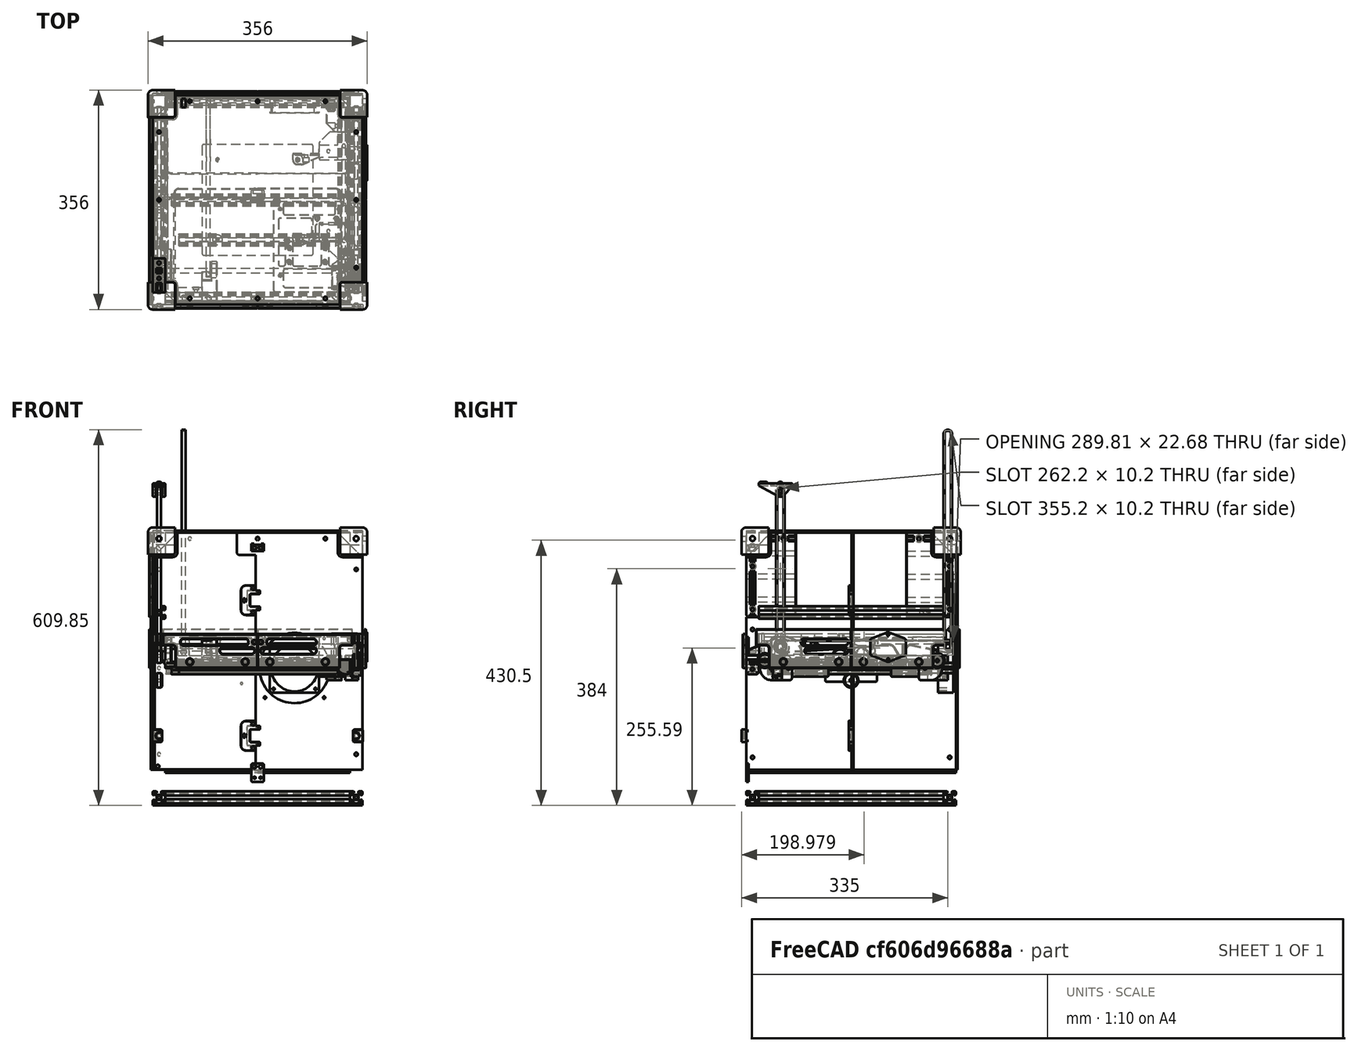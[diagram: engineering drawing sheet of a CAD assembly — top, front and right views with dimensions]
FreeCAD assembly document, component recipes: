
FREECAD ASSEMBLY — COMPONENT RECIPES ("assembly")

This assembly document has 26 components, labeled P0..P25 below (a component is one placed body or linked part). 25 of them carry a construction recipe — the FreeCAD feature program that regenerates the part from scratch, quoted from this document or its linked companion documents; the rest are supplied as boundary geometry only. No exploded tour is included for this assembly.
NOTE — this tour is split across 3 documents so each fits a 32k-token context. This is document 1: the component sections continue in the remaining 2 documents, each repeating the header above.
COMPONENT P0 — recipe-attached ("power-connector", modeled in this document).
Construction recipe (the document's own serialized feature program — sketch geometry with constraints, then the solid features built on it; lengths are millimeters unless a unit is written):

FEATURE [Sketcher::SketchObject] Sketch062
  ArcFitTolerance = 1e-06
  AttachmentSupport = -> [XZ_Plane023]
  FullyConstrained = true
  MakeInternals = false
  MapMode = 5
  Placement = pos=(0,0,0) rot=(1,0,0;1.5708rad)
  sketch-geometry (12):
    g0: LineSegment StartX=-13.225 StartY=21.3 StartZ=0 EndX=-13.225 EndY=-21.3 EndZ=0
    g1: LineSegment StartX=-11.225 StartY=-23.3 StartZ=0 EndX=11.225 EndY=-23.3 EndZ=0
    g2: LineSegment StartX=13.225 StartY=-21.3 StartZ=0 EndX=13.225 EndY=21.3 EndZ=0
    g3: LineSegment StartX=11.225 StartY=23.3 StartZ=0 EndX=-11.225 EndY=23.3 EndZ=0
    g4: ArcOfCircle CenterX=11.225 CenterY=21.3 CenterZ=0 NormalX=0 NormalY=0 NormalZ=1 AngleXU=0 Radius=2 StartAngle=1.41e-14 EndAngle=1.5708
    g5: GeomPoint [constr] X=13.225 Y=23.3 Z=0
    g6: ArcOfCircle CenterX=-11.225 CenterY=21.3 CenterZ=0 NormalX=0 NormalY=0 NormalZ=1 AngleXU=0 Radius=2 StartAngle=1.5708 EndAngle=3.14159
    g7: GeomPoint [constr] X=-13.225 Y=23.3 Z=0
    g8: ArcOfCircle CenterX=-11.225 CenterY=-21.3 CenterZ=0 NormalX=0 NormalY=0 NormalZ=1 AngleXU=0 Radius=2 StartAngle=3.14159 EndAngle=4.71239
    g9: GeomPoint [constr] X=-13.225 Y=-23.3 Z=0
    g10: ArcOfCircle CenterX=11.225 CenterY=-21.3 CenterZ=0 NormalX=0 NormalY=0 NormalZ=1 AngleXU=0 Radius=2 StartAngle=4.71239 EndAngle=6.28319
    g11: GeomPoint [constr] X=13.225 Y=-23.3 Z=0
  constraints (27):
    c: Vertical(g0)
    c: Vertical(g2)
    c: Horizontal(g1)
    c: Horizontal(g3)
    c: Symmetric(g11,g7,g-1)
    c: DistanceX(g7,g5) = 26.45
    c: DistanceY(g11,g5) = 46.6
    c: PointOnObject(g5,g2)
    c: PointOnObject(g5,g3)
    c: Tangent(g2,g4) = -1.5708
    c: Tangent(g3,g4) = -1.5708
    c: PointOnObject(g7,g0)
    c: PointOnObject(g7,g3)
    c: Tangent(g0,g6) = -1.5708
    c: Tangent(g3,g6) = -1.5708
    c: PointOnObject(g9,g0)
    c: PointOnObject(g9,g1)
    c: Tangent(g0,g8) = -1.5708
    c: Tangent(g1,g8) = -1.5708
    c: PointOnObject(g11,g1)
    c: PointOnObject(g11,g2)
    c: Tangent(g1,g10) = -1.5708
    c: Tangent(g2,g10) = -1.5708
    c: Equal(g10,g8)
    c: Equal(g8,g6)
    c: Equal(g6,g4)
    c: Radius(g4) = 2
FEATURE [PartDesign::Pad] Pad027
  Direction = (0,-1,2e-16)
  Length = 17.8
  Length2 = 10
  Placement = pos=(0,0,0) rot=(1,0,0;1.5708rad)
  Profile = -> Sketch062
  ReferenceAxis = -> Sketch062 [N_Axis]
  Reversed = true
  Suppressed = false
  Type = 0
FEATURE [Sketcher::SketchObject] Sketch063
  ArcFitTolerance = 1e-06
  AttachmentSupport = -> [XZ_Plane023]
  FullyConstrained = true
  MakeInternals = false
  MapMode = 5
  Placement = pos=(0,0,0) rot=(1,0,0;1.5708rad)
  sketch-geometry (20):
    g0: LineSegment StartX=-10.2832 StartY=29 StartZ=0 EndX=10.2832 EndY=29 EndZ=0
    g1: LineSegment StartX=14.0015 StartY=26.4745 StartZ=0 EndX=23.3306 EndY=2.94901 EndZ=0
    g2: LineSegment StartX=23.3306 StartY=-2.94901 StartZ=0 EndX=14.0015 EndY=-26.4745 EndZ=0
    g3: LineSegment StartX=10.2832 StartY=-29 StartZ=0 EndX=-10.2832 EndY=-29 EndZ=0
    g4: LineSegment StartX=-14.0015 StartY=-26.4745 StartZ=0 EndX=-23.3306 EndY=-2.94901 EndZ=0
    g5: LineSegment StartX=-23.3306 StartY=2.94901 StartZ=0 EndX=-14.0015 EndY=26.4745 EndZ=0
    g6: ArcOfCircle CenterX=-15.8939 CenterY=-3.7e-15 CenterZ=0 NormalX=0 NormalY=0 NormalZ=1 AngleXU=0 Radius=8 StartAngle=2.76406 EndAngle=3.51912
    g7: GeomPoint [constr] X=-24.5 Y=0 Z=0
    g8: ArcOfCircle CenterX=-10.2832 CenterY=25 CenterZ=0 NormalX=0 NormalY=0 NormalZ=1 AngleXU=0 Radius=4 StartAngle=1.5708 EndAngle=2.76406
    g9: GeomPoint [constr] X=-13 Y=29 Z=0
    g10: ArcOfCircle CenterX=10.2832 CenterY=25 CenterZ=0 NormalX=0 NormalY=0 NormalZ=1 AngleXU=0 Radius=4 StartAngle=0.37753 EndAngle=1.5708
    g11: GeomPoint [constr] X=13 Y=29 Z=0
    g12: ArcOfCircle CenterX=15.8939 CenterY=-2.2e-15 CenterZ=0 NormalX=0 NormalY=0 NormalZ=1 AngleXU=0 Radius=8 StartAngle=5.90566 EndAngle=6.66072
    g13: GeomPoint [constr] X=24.5 Y=0 Z=0
    g14: ArcOfCircle CenterX=10.2832 CenterY=-25 CenterZ=0 NormalX=0 NormalY=0 NormalZ=1 AngleXU=0 Radius=4 StartAngle=4.71239 EndAngle=5.90566
    g15: GeomPoint [constr] X=13 Y=-29 Z=0
    g16: ArcOfCircle CenterX=-10.2832 CenterY=-25 CenterZ=0 NormalX=0 NormalY=0 NormalZ=1 AngleXU=0 Radius=4 StartAngle=3.51912 EndAngle=4.71239
    g17: GeomPoint [constr] X=-13 Y=-29 Z=0
    g18: Circle CenterX=20 CenterY=0 CenterZ=0 NormalX=0 NormalY=0 NormalZ=1 AngleXU=0 Radius=1.75
    g19: Circle CenterX=-20 CenterY=0 CenterZ=0 NormalX=0 NormalY=0 NormalZ=1 AngleXU=0 Radius=1.75
  constraints (44):
    c: PointOnObject(g13,g-1)
    c: Horizontal(g3)
    c: Symmetric(g9,g11,g-2)
    c: Symmetric(g7,g13,g-2)
    c: Vertical(g11,g15)
    c: Symmetric(g17,g9,g-1)
    c: PointOnObject(g7,g4)
    c: PointOnObject(g7,g5)
    c: Tangent(g4,g6) = 1.5708
    c: Tangent(g5,g6) = 1.5708
    c: PointOnObject(g9,g0)
    c: PointOnObject(g9,g5)
    c: Tangent(g0,g8) = 1.5708
    c: Tangent(g5,g8) = 1.5708
    c: PointOnObject(g11,g0)
    c: PointOnObject(g11,g1)
    c: Tangent(g0,g10) = 1.5708
    c: Tangent(g1,g10) = 1.5708
    c: PointOnObject(g13,g1)
    c: PointOnObject(g13,g2)
    c: Tangent(g1,g12) = 1.5708
    c: Tangent(g2,g12) = 1.5708
    c: PointOnObject(g15,g2)
    c: PointOnObject(g15,g3)
    c: Tangent(g2,g14) = 1.5708
    c: Tangent(g3,g14) = 1.5708
    c: PointOnObject(g17,g3)
    c: PointOnObject(g17,g4)
    c: Tangent(g3,g16) = 1.5708
    c: Tangent(g4,g16) = 1.5708
    c: Equal(g16,g14)
    c: Equal(g14,g10)
    c: Equal(g10,g8)
    c: Radius(g8) = 4
    c: Equal(g6,g12)
    c: Radius(g12) = 8
    c: DistanceY(g15,g11) = 58
    c: DistanceX(g9,g11) = 26
    c: PointOnObject(g18,g-1)
    c: Symmetric(g19,g18,g-2)
    c: Equal(g18,g19)
    c: Diameter(g18) = 3.5
    c: DistanceX(g7,g13) = 49
    c: DistanceX(g19,g18) = 40
FEATURE [PartDesign::Pad] Pad112
  BaseFeature = -> Pad027
  Direction = (0,-1,2e-16)
  Length = 2
  Length2 = 10
  Placement = pos=(0,0,0) rot=(1,0,0;1.5708rad)
  Profile = -> Sketch063
  ReferenceAxis = -> Sketch063 [N_Axis]
  Suppressed = false
  Type = 0
FEATURE [PartDesign::Fillet] Fillet010
  Base = -> Pad112 [Edge60]
  BaseFeature = -> Pad112
  Placement = pos=(0,0,0) rot=(1,0,0;1.5708rad)
  Radius = 1
  SupportTransform = false
  Suppressed = false
  UseAllEdges = false
FEATURE [PartDesign::Body] Body019  label="power-connector"
  AllowCompound = false
  Group = -> [Sketch062,Pad027,Sketch063,Pad112,Fillet010]
  Origin = -> Origin023
  Placement = pos=(176,60,34) rot=(-0.58,0.58,0.58;2.0944rad)
  Tip = -> Fillet010
  expr: .Placement.Base.x = Spreadsheet.side_length / 2 + 6
COMPONENT P1 — recipe-attached ("z-motion-front-rod", modeled in this document).
Construction recipe (the document's own serialized feature program — sketch geometry with constraints, then the solid features built on it; lengths are millimeters unless a unit is written):

FEATURE [Sketcher::SketchObject] Sketch097
  ArcFitTolerance = 0
  AttachmentSupport = -> [YZ_Plane204]
  FullyConstrained = true
  MakeInternals = false
  MapMode = 5
  Placement = pos=(0,0,0) rot=(0.57735,0.57735,0.57735;2.0944rad)
  sketch-geometry (1):
    g0: Circle CenterX=0 CenterY=0 CenterZ=0 NormalX=0 NormalY=0 NormalZ=1 AngleXU=0 Radius=4
  constraints (2):
    c: Coincident(g0,g-1)
    c: Diameter(g0) = 8
FEATURE [PartDesign::Pad] Pad028
  Direction = (1,0,0)
  Length = 330
  Length2 = 10
  Midplane = true
  Placement = pos=(0,0,0) rot=(1,1,1;2.0944rad)
  Profile = -> Sketch097
  ReferenceAxis = -> Sketch097 [N_Axis]
  Suppressed = false
  Type = 0
  expr: Length = Spreadsheet.side_length - 10
FEATURE [PartDesign::Body] Body070  label="z-motion-front-rod"
  AllowCompound = false
  Group = -> [Sketch097,Pad028]
  Origin = -> Origin204
  Placement = pos=(0,-115,35) rot=(0,0,1;0rad)
  Tip = -> Pad028
  expr: .Placement.Base.y = -(Spreadsheet.side_length / 2 - 55)
COMPONENT P2 — recipe-attached ("z-motion-back-rod", modeled in this document).
Construction recipe (the document's own serialized feature program — sketch geometry with constraints, then the solid features built on it; lengths are millimeters unless a unit is written):

FEATURE [Sketcher::SketchObject] Sketch113
  ArcFitTolerance = 0
  AttachmentSupport = -> [YZ_Plane213]
  FullyConstrained = true
  MakeInternals = false
  MapMode = 5
  Placement = pos=(0,0,0) rot=(0.57735,0.57735,0.57735;2.0944rad)
  sketch-geometry (1):
    g0: Circle CenterX=0 CenterY=0 CenterZ=0 NormalX=0 NormalY=0 NormalZ=1 AngleXU=0 Radius=4
  constraints (2):
    c: Coincident(g0,g-1)
    c: Diameter(g0) = 8
FEATURE [PartDesign::Pad] Pad033
  Direction = (1,0,0)
  Length = 250
  Length2 = 10
  Midplane = true
  Placement = pos=(0,0,0) rot=(1,1,1;2.0944rad)
  Profile = -> Sketch113
  ReferenceAxis = -> Sketch113 [N_Axis]
  Suppressed = false
  Type = 0
  expr: Length = Spreadsheet.side_length - 90
FEATURE [PartDesign::Body] Body079  label="z-motion-back-rod"
  AllowCompound = false
  Group = -> [Sketch113,Pad033]
  Origin = -> Origin213
  Placement = pos=(0,157,35) rot=(0,0,1;0rad)
  Tip = -> Pad033
  expr: .Placement.Base.y = Spreadsheet.side_length / 2 - 13
COMPONENT P3 — recipe-attached ("z-motion-front-belt-right", modeled in this document).
Construction recipe (the document's own serialized feature program — sketch geometry with constraints, then the solid features built on it; lengths are millimeters unless a unit is written):

FEATURE [Sketcher::SketchObject] Sketch137
  ArcFitTolerance = 0
  AttachmentSupport = -> [YZ_Plane229]
  FullyConstrained = true
  MakeInternals = false
  MapMode = 5
  Placement = pos=(0,0,0) rot=(0.57735,0.57735,0.57735;2.0944rad)
  expr: Constraints[4] = -(Spreadsheet.side_length / 2 - 55)
  expr: Constraints[5] = Spreadsheet.xy_gantry_height - 10 - 13
  sketch-geometry (11):
    g0: Circle [constr] CenterX=-115 CenterY=35 CenterZ=0 NormalX=0 NormalY=0 NormalZ=1 AngleXU=0 Radius=6.1
    g1: Circle [constr] CenterX=-115 CenterY=287 CenterZ=0 NormalX=0 NormalY=0 NormalZ=1 AngleXU=0 Radius=6.1
    g2: ArcOfCircle CenterX=-115 CenterY=35 CenterZ=0 NormalX=0 NormalY=0 NormalZ=1 AngleXU=0 Radius=5.1 StartAngle=3.14159 EndAngle=6.28319
    g3: GeomPoint [constr] X=-108.9 Y=35 Z=0
    g4: ArcOfCircle CenterX=-115 CenterY=35 CenterZ=0 NormalX=0 NormalY=0 NormalZ=1 AngleXU=0 Radius=6.85 StartAngle=3.14159 EndAngle=6.28319
    g5: LineSegment StartX=-120.1 StartY=35 StartZ=0 EndX=-120.1 EndY=287 EndZ=0
    g6: LineSegment StartX=-121.85 StartY=35 StartZ=0 EndX=-121.85 EndY=287 EndZ=0
    g7: LineSegment StartX=-109.9 StartY=35 StartZ=0 EndX=-109.9 EndY=287 EndZ=0
    g8: LineSegment StartX=-108.15 StartY=287 StartZ=0 EndX=-108.15 EndY=35 EndZ=0
    g9: ArcOfCircle CenterX=-115 CenterY=287 CenterZ=0 NormalX=0 NormalY=0 NormalZ=1 AngleXU=0 Radius=5.1 StartAngle=6.28318 EndAngle=9.42478
    g10: ArcOfCircle CenterX=-115 CenterY=287 CenterZ=0 NormalX=0 NormalY=0 NormalZ=1 AngleXU=0 Radius=6.85 StartAngle=6.28318 EndAngle=9.42478
  constraints (32):
    c: Equal(g1,g0)
    c: Diameter(g0) = 12.2
    c: Vertical(g0,g1)
    c: DistanceY(g0) = 35
    c: DistanceX(g0) = -115
    c: DistanceY(g1) = 287
    c: Coincident(g2,g0)
    c: PointOnObject(g3,g0)
    c: Horizontal(g3,g2)
    c: Horizontal(g3,g2)
    c: DistanceX(g2,g3) = 1
    c: Coincident(g4,g2)
    c: DistanceX(g3,g4) = 0.75
    c: Horizontal(g4,g3)
    c: Horizontal(g2,g4)
    c: Horizontal(g4,g2)
    c: Coincident(g5,g2)
    c: Vertical(g5)
    c: Coincident(g6,g4)
    c: Vertical(g6)
    c: Coincident(g7,g2)
    c: Vertical(g7)
    c: Coincident(g8,g4)
    c: Vertical(g8)
    c: Coincident(g9,g1)
    c: Coincident(g9,g7)
    c: Coincident(g9,g5)
    c: Coincident(g10,g9)
    c: Coincident(g10,g6)
    c: Coincident(g10,g8)
    c: Horizontal(g9,g5)
    c: Horizontal(g5,g6)
FEATURE [PartDesign::Pad] Pad041
  Direction = (1,0,0)
  Length = 6
  Length2 = 10
  Midplane = true
  Placement = pos=(0,0,0) rot=(1,1,1;2.0944rad)
  Profile = -> Sketch137
  ReferenceAxis = -> Sketch137 [N_Axis]
  Suppressed = false
  Type = 0
FEATURE [PartDesign::Body] Body095  label="z-motion-front-belt-right"
  AllowCompound = false
  Group = -> [Sketch137,Pad041]
  Origin = -> Origin229
  Placement = pos=(160,0,0) rot=(0,0,1;0rad)
  Tip = -> Pad041
  expr: .Placement.Base.x = Spreadsheet.side_length / 2 - 10
COMPONENT P4 — recipe-attached ("z-motion-back-belt-right", modeled in this document).
Construction recipe (the document's own serialized feature program — sketch geometry with constraints, then the solid features built on it; lengths are millimeters unless a unit is written):

FEATURE [Sketcher::SketchObject] Sketch138
  ArcFitTolerance = 0
  AttachmentSupport = -> [YZ_Plane230]
  FullyConstrained = true
  MakeInternals = false
  MapMode = 5
  Placement = pos=(0,0,0) rot=(0.57735,0.57735,0.57735;2.0944rad)
  expr: Constraints[3] = Spreadsheet.side_length / 2 - 13
  expr: Constraints[5] = Spreadsheet.height - 60
  sketch-geometry (11):
    g0: Circle [constr] CenterX=157 CenterY=35 CenterZ=0 NormalX=0 NormalY=0 NormalZ=1 AngleXU=0 Radius=6.1
    g1: Circle [constr] CenterX=157 CenterY=380 CenterZ=0 NormalX=0 NormalY=0 NormalZ=1 AngleXU=0 Radius=6.1
    g2: ArcOfCircle CenterX=157 CenterY=35 CenterZ=0 NormalX=0 NormalY=0 NormalZ=1 AngleXU=0 Radius=5.1 StartAngle=3.14159 EndAngle=6.28319
    g3: ArcOfCircle CenterX=157 CenterY=35 CenterZ=0 NormalX=0 NormalY=0 NormalZ=1 AngleXU=0 Radius=6.85 StartAngle=3.14159 EndAngle=6.28319
    g4: GeomPoint [constr] X=163.1 Y=35 Z=0
    g5: LineSegment StartX=162.1 StartY=35 StartZ=0 EndX=162.1 EndY=380 EndZ=0
    g6: LineSegment StartX=163.85 StartY=35 StartZ=0 EndX=163.85 EndY=380 EndZ=0
    g7: ArcOfCircle CenterX=157 CenterY=380 CenterZ=0 NormalX=0 NormalY=0 NormalZ=1 AngleXU=0 Radius=5.1 StartAngle=-3.6e-15 EndAngle=3.14159
    g8: ArcOfCircle CenterX=157 CenterY=380 CenterZ=0 NormalX=0 NormalY=0 NormalZ=1 AngleXU=0 Radius=6.85 StartAngle=4e-16 EndAngle=3.14159
    g9: LineSegment StartX=151.9 StartY=380 StartZ=0 EndX=151.9 EndY=35 EndZ=0
    g10: LineSegment StartX=150.15 StartY=35 StartZ=0 EndX=150.15 EndY=380 EndZ=0
  constraints (30):
    c: Equal(g1,g0)
    c: Vertical(g0,g1)
    c: Diameter(g0) = 12.2
    c: DistanceX(g0) = 157
    c: DistanceY(g0) = 35
    c: DistanceY(g1) = 380
    c: Coincident(g2,g0)
    c: Horizontal(g2,g2)
    c: Horizontal(g2,g2)
    c: Coincident(g3,g2)
    c: Horizontal(g3,g3)
    c: Horizontal(g3,g2)
    c: PointOnObject(g4,g0)
    c: Horizontal(g4,g2)
    c: DistanceX(g2,g4) = 1
    c: DistanceX(g4,g3) = 0.75
    c: Coincident(g5,g2)
    c: Vertical(g5)
    c: Coincident(g6,g3)
    c: Vertical(g6)
    c: Coincident(g7,g1)
    c: Tangent(g7,g5) = -1.5708
    c: Coincident(g8,g7)
    c: Tangent(g6,g8) = -1.5708
    c: Coincident(g9,g7)
    c: Coincident(g9,g2)
    c: Vertical(g9)
    c: Coincident(g10,g3)
    c: Coincident(g10,g8)
    c: Vertical(g10)
FEATURE [PartDesign::Pad] Pad042
  Direction = (1,0,0)
  Length = 6
  Length2 = 10
  Midplane = true
  Placement = pos=(0,0,0) rot=(1,1,1;2.0944rad)
  Profile = -> Sketch138
  ReferenceAxis = -> Sketch138 [N_Axis]
  Suppressed = false
  Type = 0
FEATURE [PartDesign::Body] Body096  label="z-motion-back-belt-right"
  AllowCompound = false
  Group = -> [Sketch138,Pad042]
  Origin = -> Origin230
  Placement = pos=(120,0,0) rot=(0,0,1;0rad)
  Tip = -> Pad042
  expr: .Placement.Base.x = Spreadsheet.side_length / 2 - 50
COMPONENT P5 — recipe-attached ("z-motion-mid-belt", modeled in this document).
Construction recipe (the document's own serialized feature program — sketch geometry with constraints, then the solid features built on it; lengths are millimeters unless a unit is written):

FEATURE [Sketcher::SketchObject] Sketch168
  ArcFitTolerance = 0
  AttachmentSupport = -> [YZ_Plane243]
  FullyConstrained = false
  MakeInternals = false
  MapMode = 5
  Placement = pos=(0,0,0) rot=(0.57735,0.57735,0.57735;2.0944rad)
  expr: Constraints[0] = Spreadsheet.side_length / 2 - 90
  expr: Constraints[13] = -(Spreadsheet.side_length / 2 - 55)
  expr: Constraints[14] = Spreadsheet.side_length / 2 - 13
  sketch-geometry (31):
    g0: Circle [constr] CenterX=-115 CenterY=35 CenterZ=0 NormalX=0 NormalY=0 NormalZ=1 AngleXU=0 Radius=9.93
    g1: Circle [constr] CenterX=157 CenterY=35 CenterZ=0 NormalX=0 NormalY=0 NormalZ=1 AngleXU=0 Radius=9.93
    g2: Circle [constr] CenterX=80 CenterY=25 CenterZ=0 NormalX=0 NormalY=0 NormalZ=1 AngleXU=0 Radius=4.75
    g3: Circle [constr] CenterX=97 CenterY=30 CenterZ=0 NormalX=0 NormalY=0 NormalZ=1 AngleXU=0 Radius=6.5
    g4: Circle [constr] CenterX=63 CenterY=30 CenterZ=0 NormalX=0 NormalY=0 NormalZ=1 AngleXU=0 Radius=6.5
    g5: GeomPoint [constr] X=80 Y=30 Z=0
    g6: ArcOfCircle CenterX=-115 CenterY=35 CenterZ=0 NormalX=0 NormalY=0 NormalZ=1 AngleXU=0 Radius=8.93 StartAngle=1.5708 EndAngle=4.78094
    g7: ArcOfCircle CenterX=-115 CenterY=35 CenterZ=0 NormalX=0 NormalY=0 NormalZ=1 AngleXU=0 Radius=10.68 StartAngle=1.5708 EndAngle=4.78094
    g8: GeomPoint [constr] X=-115 Y=44.93 Z=0
    g9: LineSegment StartX=-114.268 StartY=24.3451 StartZ=0 EndX=62.5548 EndY=36.4847 EndZ=0
    g10: LineSegment StartX=-114.388 StartY=26.091 StartZ=0 EndX=62.4349 EndY=38.2306 EndZ=0
    g11: ArcOfCircle CenterX=63 CenterY=30 CenterZ=0 NormalX=0 NormalY=0 NormalZ=1 AngleXU=0 Radius=6.5 StartAngle=0.540795 EndAngle=1.63934
    g12: ArcOfCircle CenterX=63 CenterY=30 CenterZ=0 NormalX=0 NormalY=0 NormalZ=1 AngleXU=0 Radius=8.25 StartAngle=0.540795 EndAngle=1.63934
    g13: LineSegment StartX=70.0727 StartY=34.2472 StartZ=0 EndX=76.7851 EndY=23.0694 EndZ=0
    g14: LineSegment StartX=68.5724 StartY=33.3463 StartZ=0 EndX=75.2849 EndY=22.1685 EndZ=0
    g15: ArcOfCircle CenterX=80 CenterY=25 CenterZ=0 NormalX=0 NormalY=0 NormalZ=1 AngleXU=0 Radius=3.75 StartAngle=3.68239 EndAngle=5.74239
    g16: ArcOfCircle CenterX=80 CenterY=25 CenterZ=0 NormalX=0 NormalY=0 NormalZ=1 AngleXU=0 Radius=5.5 StartAngle=3.68239 EndAngle=5.74239
    g17: GeomPoint [constr] X=80 Y=20.25 Z=0
    g18: GeomPoint [constr] X=80 Y=21.25 Z=0
    g19: LineSegment StartX=84.7151 StartY=22.1685 StartZ=0 EndX=91.4276 EndY=33.3463 EndZ=0
    g20: LineSegment StartX=83.2149 StartY=23.0694 StartZ=0 EndX=89.9273 EndY=34.2472 EndZ=0
    g21: ArcOfCircle CenterX=97 CenterY=30 CenterZ=0 NormalX=0 NormalY=0 NormalZ=1 AngleXU=0 Radius=6.5 StartAngle=1.36457 EndAngle=2.6008
    g22: ArcOfCircle CenterX=97 CenterY=30 CenterZ=0 NormalX=0 NormalY=0 NormalZ=1 AngleXU=0 Radius=8.25 StartAngle=1.36457 EndAngle=2.6008
    g23: LineSegment StartX=98.331 StartY=36.3623 StartZ=0 EndX=154.813 EndY=24.5463 EndZ=0
    g24: LineSegment StartX=98.6893 StartY=38.0752 StartZ=0 EndX=155.171 EndY=26.2592 EndZ=0
    g25: ArcOfCircle CenterX=157 CenterY=35 CenterZ=0 NormalX=0 NormalY=0 NormalZ=1 AngleXU=0 Radius=8.93 StartAngle=4.50616 EndAngle=7.85398
    g26: ArcOfCircle CenterX=157 CenterY=35 CenterZ=0 NormalX=0 NormalY=0 NormalZ=1 AngleXU=0 Radius=10.68 StartAngle=4.50616 EndAngle=7.85398
    g27: LineSegment StartX=157 StartY=43.93 StartZ=0 EndX=-115 EndY=43.93 EndZ=0
    g28: LineSegment StartX=-115 StartY=45.68 StartZ=0 EndX=157 EndY=45.68 EndZ=0
    g29: LineSegment [constr] StartX=-106.078 StartY=46.712 StartZ=0 EndX=149.922 EndY=46.712 EndZ=0
    g30: LineSegment [constr] StartX=62.8347 StartY=47.5455 StartZ=0 EndX=86.8427 EndY=47.5455 EndZ=0
  constraints (71):
    c: DistanceX(g2) = 80
    c: DistanceY(g2) = 25
    c: Diameter(g2) = 9.5
    c: Symmetric(g3,g4,g5)
    c: Horizontal(g4,g3)
    c: Vertical(g5,g2)
    c: Equal(g4,g3)
    c: DistanceX(g4,g3) = 34
    c: DistanceY(g3) = 30
    c: Diameter(g3) = 13
    c: Horizontal(g1,g0)
    c: DistanceY(g0) = 35
    c: Diameter(g0) = 19.86
    c: DistanceX(g0) = -115
    c: DistanceX(g1) = 157
    c: Equal(g1,g0)
    c: Coincident(g6,g0)
    c: Coincident(g7,g6)
    c: PointOnObject(g8,g0)
    c: Vertical(g6,g8)
    c: Vertical(g8,g7)
    c: Vertical(g7,g6)
    c: DistanceY(g6,g8) = 1
    c: DistanceY(g8,g7) = 0.75
    c: PointOnObject(g9,g4)
    c: Tangent(g9,g4)
    c: Coincident(g11,g4)
    c: Coincident(g11,g9)
    c: Coincident(g12,g11)
    c: Coincident(g15,g2)
    c: Coincident(g16,g15)
    c: Tangent(g10,g6) = -1.5708
    c: Tangent(g9,g7) = -1.5708
    c: Parallel(g10,g9)
    c: Tangent(g12,g10) = 1.5708
    c: Tangent(g13,g12) = 1.5708
    c: Tangent(g14,g11) = 1.5708
    c: Parallel(g14,g13)
    c: Tangent(g15,g13) = -1.5708
    c: Tangent(g16,g14) = -1.5708
    c: PointOnObject(g17,g2)
    c: PointOnObject(g18,g15)
    c: Vertical(g17,g18)
    c: Vertical(g18,g15)
    c: DistanceY(g17,g18) = 1
    c: PointOnObject(g19,g3)
    c: Tangent(g19,g3)
    c: Tangent(g19,g16) = -1.5708
    c: Tangent(g20,g15) = -1.5708
    c: Parallel(g19,g20)
    c: Coincident(g21,g3)
    c: Coincident(g21,g19)
    c: Coincident(g22,g21)
    c: Tangent(g22,g20) = 1.5708
    c: Coincident(g23,g21)
    c: Tangent(g23,g3)
    c: Tangent(g24,g22) = 1.5708
    c: Parallel(g23,g24)
    c: Coincident(g25,g1)
    c: Coincident(g26,g25)
    c: Tangent(g26,g23) = -1.5708
    c: Tangent(g25,g24) = -1.5708
    c: Coincident(g27,g6)
    c: Horizontal(g27)
    c: Coincident(g28,g7)
    c: Coincident(g28,g26)
    c: Horizontal(g28)
    c: Tangent(g27,g25) = -1.5708
    c: Horizontal(g29)
    c: DistanceX(g29,g29) = 256
    c: Horizontal(g30)
FEATURE [PartDesign::Pad] Pad048
  Direction = (1,0,0)
  Length = 6
  Length2 = 10
  Midplane = true
  Placement = pos=(0,0,0) rot=(1,1,1;2.0944rad)
  Profile = -> Sketch168
  ReferenceAxis = -> Sketch168 [N_Axis]
  Suppressed = false
  Type = 0
FEATURE [PartDesign::Body] Body110  label="z-motion-mid-belt"
  AllowCompound = false
  Group = -> [Sketch168,Pad048]
  Origin = -> Origin244
  Placement = pos=(-80,0,0) rot=(0,0,1;0rad)
  Tip = -> Pad048
  expr: .Placement.Base.x = -(Spreadsheet.side_length / 2 - 90)
COMPONENT P6 — recipe-attached ("z-motion-bearing-block-mid", modeled in this document).
Construction recipe (the document's own serialized feature program — sketch geometry with constraints, then the solid features built on it; lengths are millimeters unless a unit is written):

FEATURE [Sketcher::SketchObject] Sketch395
  ArcFitTolerance = 1e-06
  AttachmentOffset = pos=(0,0,80) rot=(0,0,1;0rad)
  AttachmentSupport = -> [YZ_Plane266]
  FullyConstrained = true
  MakeInternals = false
  MapMode = 5
  Placement = pos=(80,0,0) rot=(0.57735,0.57735,0.57735;2.0944rad)
  sketch-geometry (17):
    g0: LineSegment StartX=20 StartY=2 StartZ=0 EndX=20 EndY=20 EndZ=0
    g1: LineSegment StartX=20 StartY=20 StartZ=0 EndX=2 EndY=20 EndZ=0
    g2: LineSegment StartX=0 StartY=22 StartZ=0 EndX=0 EndY=26.675 EndZ=0
    g3: LineSegment StartX=1.22015 StartY=28.5167 StartZ=0 EndX=49.1511 EndY=48.8127 EndZ=0
    g4: ArcOfCircle CenterX=55 CenterY=35 CenterZ=0 NormalX=0 NormalY=0 NormalZ=1 AngleXU=0 Radius=15 StartAngle=5.2799 EndAngle=8.25453
    g5: LineSegment StartX=63.063 StartY=22.3514 StartZ=0 EndX=28.4918 EndY=0.313517 EndZ=0
    g6: LineSegment StartX=22 StartY=4e-16 StartZ=0 EndX=27.4168 EndY=0 EndZ=0
    g7: Circle CenterX=55 CenterY=35 CenterZ=0 NormalX=0 NormalY=0 NormalZ=1 AngleXU=0 Radius=9
    g8: ArcOfCircle CenterX=2 CenterY=26.675 CenterZ=0 NormalX=0 NormalY=0 NormalZ=1 AngleXU=0 Radius=2 StartAngle=1.97135 EndAngle=3.14159
    g9: GeomPoint [constr] X=0 Y=28 Z=0
    g10: ArcOfCircle CenterX=2 CenterY=22 CenterZ=0 NormalX=0 NormalY=0 NormalZ=1 AngleXU=0 Radius=2 StartAngle=3.14159 EndAngle=4.71239
    g11: GeomPoint [constr] X=0 Y=20 Z=0
    g12: ArcOfCircle CenterX=22 CenterY=2 CenterZ=0 NormalX=0 NormalY=0 NormalZ=1 AngleXU=0 Radius=2 StartAngle=3.14159 EndAngle=4.71239
    g13: GeomPoint [constr] X=20 Y=0 Z=0
    g14: ArcOfCircle CenterX=27.4168 CenterY=2 CenterZ=0 NormalX=0 NormalY=0 NormalZ=1 AngleXU=0 Radius=2 StartAngle=4.71239 EndAngle=5.2799
    g15: GeomPoint [constr] X=28 Y=0 Z=0
    g16: GeomPoint X=55 Y=50 Z=0
  constraints (40):
    c: PointOnObject(g13,g-1)
    c: Vertical(g0)
    c: Coincident(g0,g1)
    c: PointOnObject(g11,g-2)
    c: Horizontal(g1)
    c: PointOnObject(g9,g-2)
    c: PointOnObject(g15,g-1)
    c: DistanceY(g13,g0) = 20
    c: Tangent(g4,g3) = 1.5708
    c: Tangent(g5,g4) = 1.5708
    c: DistanceX(g4) = 55
    c: DistanceY(g4) = 35
    c: DistanceY(g9) = 28
    c: DistanceX(g15) = 28
    c: Coincident(g7,g4)
    c: Diameter(g7) = 18
    c: PointOnObject(g9,g2)
    c: PointOnObject(g9,g3)
    c: Tangent(g2,g8) = 1.5708
    c: Tangent(g3,g8) = 1.5708
    c: PointOnObject(g11,g1)
    c: PointOnObject(g11,g2)
    c: Tangent(g1,g10) = 1.5708
    c: Tangent(g2,g10) = 1.5708
    c: PointOnObject(g13,g0)
    c: PointOnObject(g13,g6)
    c: Tangent(g0,g12) = 1.5708
    c: Tangent(g6,g12) = -1.5708
    c: PointOnObject(g15,g5)
    c: PointOnObject(g15,g6)
    c: Tangent(g5,g14) = 1.5708
    c: Tangent(g6,g14) = -1.5708
    c: Equal(g14,g12)
    c: Equal(g14,g10)
    c: Equal(g14,g8)
    c: Radius(g14) = 2
    c: DistanceX(g0) = 20
    c: PointOnObject(g16,g4)
    c: Vertical(g16,g4)
    c: DistanceY(g16) = 50
FEATURE [PartDesign::Pad] Pad084
  Direction = (1,0,0)
  Length = 24
  Length2 = 10
  Placement = pos=(0,0,0) rot=(1,1,1;2.0944rad)
  Profile = -> Sketch395
  ReferenceAxis = -> Sketch395 [N_Axis]
  Suppressed = false
  Type = 0
FEATURE [Sketcher::SketchObject] Sketch396
  ArcFitTolerance = 1e-06
  AttachmentOffset = pos=(0,0,95) rot=(0,0,1;0rad)
  AttachmentSupport = -> [YZ_Plane266]
  FullyConstrained = true
  MakeInternals = false
  MapMode = 5
  Placement = pos=(95,0,0) rot=(0.57735,0.57735,0.57735;2.0944rad)
  sketch-geometry (1):
    g0: Circle CenterX=55 CenterY=35 CenterZ=0 NormalX=0 NormalY=0 NormalZ=1 AngleXU=0 Radius=16
  constraints (3):
    c: DistanceX(g0) = 55
    c: DistanceY(g0) = 35
    c: Diameter(g0) = 32
FEATURE [PartDesign::Pocket] Pocket275
  BaseFeature = -> Pad084
  Direction = (-1,0,0)
  Length = 5
  Length2 = 5
  Placement = pos=(0,0,0) rot=(1,1,1;2.0944rad)
  Profile = -> Sketch396
  ReferenceAxis = -> Sketch396 [N_Axis]
  Suppressed = false
  Type = 1
FEATURE [Sketcher::SketchObject] Sketch397
  ArcFitTolerance = 1e-06
  AttachmentSupport = -> [YZ_Plane266]
  FullyConstrained = true
  MakeInternals = false
  MapMode = 5
  Placement = pos=(0,0,0) rot=(0.57735,0.57735,0.57735;2.0944rad)
  sketch-geometry (15):
    g0: LineSegment StartX=2 StartY=20 StartZ=0 EndX=20 EndY=20 EndZ=0
    g1: LineSegment StartX=20 StartY=20 StartZ=0 EndX=20 EndY=2 EndZ=0
    g2: LineSegment StartX=22 StartY=0 StartZ=0 EndX=26 EndY=0 EndZ=0
    g3: LineSegment StartX=28 StartY=2 StartZ=0 EndX=28 EndY=20 EndZ=0
    g4: ArcOfCircle CenterX=20 CenterY=20 CenterZ=0 NormalX=0 NormalY=0 NormalZ=1 AngleXU=0 Radius=8 StartAngle=2e-16 EndAngle=1.5708
    g5: LineSegment StartX=20 StartY=28 StartZ=0 EndX=2 EndY=28 EndZ=0
    g6: LineSegment StartX=0 StartY=26 StartZ=0 EndX=0 EndY=22 EndZ=0
    g7: ArcOfCircle CenterX=2 CenterY=22 CenterZ=0 NormalX=0 NormalY=0 NormalZ=1 AngleXU=0 Radius=2 StartAngle=3.14159 EndAngle=4.71239
    g8: GeomPoint [constr] X=0 Y=20 Z=0
    g9: ArcOfCircle CenterX=2 CenterY=26 CenterZ=0 NormalX=0 NormalY=0 NormalZ=1 AngleXU=0 Radius=2 StartAngle=1.5708 EndAngle=3.14159
    g10: GeomPoint [constr] X=0 Y=28 Z=0
    g11: ArcOfCircle CenterX=26 CenterY=2 CenterZ=0 NormalX=0 NormalY=0 NormalZ=1 AngleXU=0 Radius=2 StartAngle=4.71239 EndAngle=6.28319
    g12: GeomPoint [constr] X=28 Y=0 Z=0
    g13: ArcOfCircle CenterX=22 CenterY=2 CenterZ=0 NormalX=0 NormalY=0 NormalZ=1 AngleXU=0 Radius=2 StartAngle=3.14159 EndAngle=4.71239
    g14: GeomPoint [constr] X=20 Y=0 Z=0
  constraints (35):
    c: PointOnObject(g8,g-2)
    c: Horizontal(g0)
    c: Coincident(g0,g1)
    c: PointOnObject(g14,g-1)
    c: Vertical(g1)
    c: PointOnObject(g12,g-1)
    c: Vertical(g3)
    c: Coincident(g4,g0)
    c: Tangent(g4,g5) = -1.5708
    c: Vertical(g6)
    c: Horizontal(g5)
    c: Tangent(g4,g3) = -1.5708
    c: DistanceX(g8,g0) = 20
    c: DistanceY(g10) = 28
    c: PointOnObject(g8,g6)
    c: PointOnObject(g8,g0)
    c: Tangent(g6,g7) = -1.5708
    c: Tangent(g0,g7) = -1.5708
    c: PointOnObject(g10,g6)
    c: PointOnObject(g10,g5)
    c: Tangent(g6,g9) = -1.5708
    c: Tangent(g5,g9) = -1.5708
    c: PointOnObject(g12,g3)
    c: PointOnObject(g12,g2)
    c: Tangent(g3,g11) = -1.5708
    c: Tangent(g2,g11) = -1.5708
    c: PointOnObject(g14,g2)
    c: PointOnObject(g14,g1)
    c: Tangent(g2,g13) = -1.5708
    c: Tangent(g1,g13) = -1.5708
    c: Equal(g7,g9)
    c: Equal(g7,g11)
    c: Equal(g7,g13)
    c: Radius(g7) = 2
    c: DistanceY(g0) = 20
FEATURE [PartDesign::Pad] Pad085
  BaseFeature = -> Pocket275
  Direction = (1,0,0)
  Length = 80
  Length2 = -40.2
  Placement = pos=(0,0,0) rot=(1,1,1;2.0944rad)
  Profile = -> Sketch397
  ReferenceAxis = -> Sketch397 [N_Axis]
  Refine = true
  Suppressed = false
  Type = 4
FEATURE [Sketcher::SketchObject] Sketch398
  ArcFitTolerance = 1e-06
  AttachmentOffset = pos=(0,0,103) rot=(0,0,1;0rad)
  AttachmentSupport = -> [YZ_Plane266]
  FullyConstrained = true
  MakeInternals = false
  MapMode = 5
  Placement = pos=(103,0,0) rot=(0.57735,0.57735,0.57735;2.0944rad)
  sketch-geometry (1):
    g0: Circle CenterX=55 CenterY=35 CenterZ=0 NormalX=0 NormalY=0 NormalZ=1 AngleXU=0 Radius=11
  constraints (3):
    c: DistanceX(g0) = 55
    c: DistanceY(g0) = 35
    c: Diameter(g0) = 22
FEATURE [PartDesign::Pocket] Pocket276
  BaseFeature = -> Pad085
  Direction = (-1,0,0)
  Length = 5
  Length2 = 5
  Placement = pos=(0,0,0) rot=(1,1,1;2.0944rad)
  Profile = -> Sketch398
  ReferenceAxis = -> Sketch398 [N_Axis]
  Suppressed = false
  Type = 1
FEATURE [Sketcher::SketchObject] Sketch401
  ArcFitTolerance = 1e-06
  AttachmentOffset = pos=(0,0,24) rot=(0,0,1;0rad)
  AttachmentSupport = -> [XY_Plane266]
  FullyConstrained = true
  MakeInternals = false
  MapMode = 5
  Placement = pos=(0,0,24) rot=(0,0,1;0rad)
  sketch-geometry (2):
    g0: Circle CenterX=90 CenterY=10 CenterZ=0 NormalX=0 NormalY=0 NormalZ=1 AngleXU=0 Radius=5
    g1: Circle CenterX=50 CenterY=10 CenterZ=0 NormalX=0 NormalY=0 NormalZ=1 AngleXU=0 Radius=5
  constraints (6):
    c: DistanceX(g0) = 90
    c: DistanceY(g0) = 10
    c: Diameter(g0) = 10
    c: Horizontal(g1,g0)
    c: DistanceX(g1) = 50
    c: Equal(g1,g0)
FEATURE [PartDesign::Pocket] Pocket277
  BaseFeature = -> Pocket276
  Direction = (0,0,-1)
  Length = 5
  Length2 = 5
  Placement = pos=(0,0,0) rot=(1,1,1;2.0944rad)
  Profile = -> Sketch401
  ReferenceAxis = -> Sketch401 [N_Axis]
  Reversed = true
  Suppressed = false
  Type = 1
FEATURE [Sketcher::SketchObject] Sketch402
  ArcFitTolerance = 1e-06
  AttachmentSupport = -> [XY_Plane266]
  FullyConstrained = true
  MakeInternals = false
  MapMode = 5
  sketch-geometry (2):
    g0: Circle CenterX=90 CenterY=10 CenterZ=0 NormalX=0 NormalY=0 NormalZ=1 AngleXU=0 Radius=2.75
    g1: Circle CenterX=50 CenterY=10 CenterZ=0 NormalX=0 NormalY=0 NormalZ=1 AngleXU=0 Radius=2.75
  constraints (6):
    c: DistanceY(g0) = 10
    c: DistanceX(g0) = 90
    c: Diameter(g0) = 5.5
    c: Horizontal(g1,g0)
    c: Equal(g1,g0)
    c: DistanceX(g1) = 50
FEATURE [PartDesign::Pocket] Pocket278
  BaseFeature = -> Pocket277
  Direction = (0,0,-1)
  Length = 5
  Length2 = 5
  Midplane = true
  Placement = pos=(0,0,0) rot=(1,1,1;2.0944rad)
  Profile = -> Sketch402
  ReferenceAxis = -> Sketch402 [N_Axis]
  Suppressed = false
  Type = 1
FEATURE [Sketcher::SketchObject] Sketch403
  ArcFitTolerance = 1e-06
  AttachmentOffset = pos=(0,0,-24) rot=(0,0,1;0rad)
  AttachmentSupport = -> [XZ_Plane266]
  FullyConstrained = true
  MakeInternals = false
  MapMode = 5
  Placement = pos=(0,24,-5.3e-15) rot=(1,0,0;1.5708rad)
  sketch-geometry (1):
    g0: Circle CenterX=70 CenterY=10 CenterZ=0 NormalX=0 NormalY=0 NormalZ=1 AngleXU=0 Radius=5
  constraints (3):
    c: DistanceX(g0) = 70
    c: DistanceY(g0) = 10
    c: Diameter(g0) = 10
FEATURE [PartDesign::Pocket] Pocket279
  BaseFeature = -> Pocket278
  Direction = (0,1,-2e-16)
  Length = 5
  Length2 = 5
  Placement = pos=(0,0,0) rot=(1,1,1;2.0944rad)
  Profile = -> Sketch403
  ReferenceAxis = -> Sketch403 [N_Axis]
  Suppressed = false
  Type = 1
FEATURE [Sketcher::SketchObject] Sketch404
  ArcFitTolerance = 1e-06
  AttachmentSupport = -> [XZ_Plane266]
  FullyConstrained = true
  MakeInternals = false
  MapMode = 5
  Placement = pos=(0,0,0) rot=(1,0,0;1.5708rad)
  sketch-geometry (1):
    g0: Circle CenterX=70 CenterY=10 CenterZ=0 NormalX=0 NormalY=0 NormalZ=1 AngleXU=0 Radius=2.75
  constraints (3):
    c: DistanceY(g0) = 10
    c: DistanceX(g0) = 70
    c: Diameter(g0) = 5.5
FEATURE [PartDesign::Pocket] Pocket280
  BaseFeature = -> Pocket279
  Direction = (0,1,-2e-16)
  Length = 5
  Length2 = 5
  Midplane = true
  Placement = pos=(0,0,0) rot=(1,1,1;2.0944rad)
  Profile = -> Sketch404
  ReferenceAxis = -> Sketch404 [N_Axis]
  Suppressed = false
  Type = 1
FEATURE [PartDesign::Fillet] Fillet008
  Base = -> Pocket280 [Edge66,Edge73]
  BaseFeature = -> Pocket280
  Placement = pos=(0,0,0) rot=(1,1,1;2.0944rad)
  Radius = 2
  SupportTransform = false
  Suppressed = false
  UseAllEdges = false
FEATURE [PartDesign::Chamfer] Chamfer018
  Angle = 45
  Base = -> Fillet008 [Face17]
  BaseFeature = -> Fillet008
  ChamferType = 0
  FlipDirection = false
  Placement = pos=(0,0,0) rot=(1,1,1;2.0944rad)
  Size = 0.75
  Size2 = 1
  SupportTransform = false
  Suppressed = false
  UseAllEdges = false
FEATURE [PartDesign::Body] Body131  label="z-motion-bearing-block-mid"
  AllowCompound = false
  Group = -> [Sketch395,Pad084,Sketch396,Pocket275,Sketch397,Pad085,Sketch398,Pocket276,Sketch401,Pocket277,Sketch402,Pocket278,Sketch403,Pocket279,Sketch404,Pocket280,Fillet008,Chamfer018]
  Origin = -> Origin267
  Placement = pos=(-170,-170,0) rot=(0,0,1;0rad)
  Tip = -> Chamfer018
  expr: .Placement.Base.x = -Spreadsheet.side_length / 2
  expr: .Placement.Base.y = -Spreadsheet.side_length / 2
COMPONENT P7 — recipe-attached ("skirt-right-back-drv", modeled in this document).
Construction recipe (the document's own serialized feature program — sketch geometry with constraints, then the solid features built on it; lengths are millimeters unless a unit is written):

FEATURE [Sketcher::SketchObject] Sketch408
  ArcFitTolerance = 1e-06
  AttachmentSupport = -> [YZ_Plane268]
  FullyConstrained = true
  MakeInternals = false
  MapMode = 5
  Placement = pos=(0,0,0) rot=(0.57735,0.57735,0.57735;2.0944rad)
  expr: Constraints[20] = Spreadsheet.side_length / 2
  sketch-geometry (9):
    g0: LineSegment StartX=0 StartY=0 StartZ=0 EndX=133.5 EndY=0 EndZ=0
    g1: LineSegment StartX=133.5 StartY=0 StartZ=0 EndX=133.5 EndY=32.5 EndZ=0
    g2: LineSegment StartX=137.5 StartY=36.5 StartZ=0 EndX=154 EndY=36.5 EndZ=0
    g3: LineSegment StartX=154 StartY=36.5 StartZ=0 EndX=154 EndY=55 EndZ=0
    g4: LineSegment StartX=154 StartY=55 StartZ=0 EndX=0 EndY=55 EndZ=0
    g5: LineSegment StartX=0 StartY=55 StartZ=0 EndX=0 EndY=0 EndZ=0
    g6: ArcOfCircle CenterX=137.5 CenterY=32.5 CenterZ=0 NormalX=0 NormalY=0 NormalZ=1 AngleXU=0 Radius=4 StartAngle=1.5708 EndAngle=3.14159
    g7: GeomPoint [constr] X=133.5 Y=36.5 Z=0
    g8: GeomPoint X=170 Y=0 Z=0
  constraints (23):
    c: Coincident(g-1,g0)
    c: PointOnObject(g0,g-1)
    c: Coincident(g0,g1)
    c: Vertical(g1)
    c: Coincident(g2,g3)
    c: Vertical(g3)
    c: Coincident(g3,g4)
    c: PointOnObject(g4,g-2)
    c: Horizontal(g4)
    c: Coincident(g4,g5)
    c: Coincident(g5,g0)
    c: Horizontal(g2)
    c: PointOnObject(g7,g1)
    c: PointOnObject(g7,g2)
    c: Tangent(g1,g6) = 1.5708
    c: Tangent(g2,g6) = 1.5708
    c: Radius(g6) = 4
    c: DistanceY(g2) = 36.5
    c: DistanceY(g4) = 55
    c: PointOnObject(g8,g-1)
    c: DistanceX(g8) = 170
    c: DistanceX(g2,g8) = 16
    c: DistanceX(g0,g8) = 36.5
FEATURE [PartDesign::Pad] Pad089
  Direction = (1,0,0)
  Length = 6
  Length2 = 24
  Placement = pos=(0,0,0) rot=(1,1,1;2.0944rad)
  Profile = -> Sketch408
  ReferenceAxis = -> Sketch408 [N_Axis]
  Suppressed = false
  Type = 4
FEATURE [Sketcher::SketchObject] Sketch409
  ArcFitTolerance = 1e-06
  AttachmentSupport = -> [XZ_Plane268]
  FullyConstrained = true
  MakeInternals = false
  MapMode = 5
  Placement = pos=(0,0,0) rot=(1,0,0;1.5708rad)
  sketch-geometry (17):
    g0: LineSegment StartX=0 StartY=0 StartZ=0 EndX=0 EndY=5.72426 EndZ=0
    g1: LineSegment StartX=0 StartY=5.72426 StartZ=0 EndX=-2 EndY=7.72426 EndZ=0
    g2: LineSegment StartX=-2 StartY=7.72426 StartZ=0 EndX=-2 EndY=12.2757 EndZ=0
    g3: LineSegment StartX=-2 StartY=12.2757 StartZ=0 EndX=0 EndY=14.2757 EndZ=0
    g4: LineSegment StartX=0 StartY=14.2757 StartZ=0 EndX=0 EndY=20 EndZ=0
    g5: LineSegment [constr] StartX=0 StartY=20 StartZ=0 EndX=-24 EndY=20 EndZ=0
    g6: LineSegment StartX=-24 StartY=20 StartZ=0 EndX=-24 EndY=0 EndZ=0
    g7: LineSegment StartX=-24 StartY=0 StartZ=0 EndX=0 EndY=0 EndZ=0
    g8: GeomPoint X=0 Y=10 Z=0
    g9: GeomPoint X=-2 Y=10 Z=0
    g10: LineSegment [constr] StartX=-2 StartY=12.7 StartZ=0 EndX=-2 EndY=7.3 EndZ=0
    g11: LineSegment StartX=-24 StartY=55 StartZ=0 EndX=-24 EndY=50 EndZ=0
    g12: LineSegment StartX=-24 StartY=50 StartZ=0 EndX=-20 EndY=50 EndZ=0
    g13: LineSegment StartX=-20 StartY=50 StartZ=0 EndX=-20 EndY=55 EndZ=0
    g14: LineSegment StartX=-20 StartY=55 StartZ=0 EndX=-24 EndY=55 EndZ=0
    g15: LineSegment StartX=0 StartY=20 StartZ=0 EndX=-24 EndY=44 EndZ=0
    g16: LineSegment StartX=-24 StartY=44 StartZ=0 EndX=-24 EndY=20 EndZ=0
  constraints (45):
    c: Coincident(g-1,g0)
    c: PointOnObject(g0,g-2)
    c: Coincident(g0,g1)
    c: Coincident(g1,g2)
    c: Vertical(g2)
    c: Coincident(g2,g3)
    c: PointOnObject(g3,g-2)
    c: Coincident(g3,g4)
    c: PointOnObject(g4,g-2)
    c: Coincident(g4,g5)
    c: Horizontal(g5)
    c: Coincident(g5,g6)
    c: PointOnObject(g6,g-1)
    c: Vertical(g6)
    c: Coincident(g6,g7)
    c: Coincident(g7,g0)
    c: DistanceX(g7,g7) = 24
    c: DistanceY(g6,g6) = 20
    c: Symmetric(g4,g0,g8)
    c: Perpendicular(g1,g3)
    c: DistanceX(g1,g1) = 2
    c: Symmetric(g2,g2,g9)
    c: Horizontal(g9,g8)
    c: Angle(g1) = 2.35619
    c: Vertical(g10)
    c: Symmetric(g10,g10,g9)
    c: DistanceY(g10,g10) = 5.4
    c: Distance(g10,g3) = 0.3
    c: Coincident(g11,g12)
    c: Coincident(g12,g13)
    c: Coincident(g13,g14)
    c: Coincident(g14,g11)
    c: Vertical(g11)
    c: Vertical(g13)
    c: Horizontal(g12)
    c: Horizontal(g14)
    c: Vertical(g11,g5)
    c: DistanceX(g12) = -20
    c: DistanceY(g12) = 50
    c: DistanceY(g13) = 55
    c: Coincident(g15,g16)
    c: Coincident(g16,g5)
    c: Vertical(g16)
    c: Angle(g15) = 2.35619
    c: Coincident(g15,g4)
FEATURE [PartDesign::Pocket] Pocket283
  BaseFeature = -> Pad089
  Direction = (0,1,-2e-16)
  Length = 5
  Length2 = 5
  Midplane = true
  Placement = pos=(0,0,0) rot=(1,1,1;2.0944rad)
  Profile = -> Sketch409
  ReferenceAxis = -> Sketch409 [N_Axis]
  Suppressed = false
  Type = 1
FEATURE [Sketcher::SketchObject] Sketch410
  ArcFitTolerance = 1e-06
  AttachmentSupport = -> [XY_Plane268]
  FullyConstrained = true
  MakeInternals = false
  MapMode = 5
  expr: Constraints[10] = Spreadsheet.side_length / 2
  sketch-geometry (15):
    g0: LineSegment StartX=-24 StartY=170 StartZ=0 EndX=-24 EndY=149.7 EndZ=0
    g1: LineSegment StartX=-24 StartY=149.7 StartZ=0 EndX=-14.5757 EndY=149.7 EndZ=0
    g2: LineSegment StartX=0 StartY=149.7 StartZ=0 EndX=0 EndY=170 EndZ=0
    g3: LineSegment StartX=0 StartY=170 StartZ=0 EndX=-24 EndY=170 EndZ=0
    g4: LineSegment [constr] StartX=-20 StartY=170 StartZ=0 EndX=-20 EndY=150 EndZ=0
    g5: LineSegment [constr] StartX=-20 StartY=150 StartZ=0 EndX=0 EndY=150 EndZ=0
    g6: LineSegment [constr] StartX=0 StartY=150 StartZ=0 EndX=0 EndY=170 EndZ=0
    g7: LineSegment [constr] StartX=0 StartY=170 StartZ=0 EndX=-20 EndY=170 EndZ=0
    g8: GeomPoint [constr] X=-10 Y=150 Z=0
    g9: LineSegment StartX=-14.5757 StartY=149.7 StartZ=0 EndX=-12.2757 EndY=152 EndZ=0
    g10: LineSegment StartX=-12.2757 StartY=152 StartZ=0 EndX=-7.72426 EndY=152 EndZ=0
    g11: LineSegment StartX=-7.72426 StartY=152 StartZ=0 EndX=-5.42426 EndY=149.7 EndZ=0
    g12: GeomPoint X=-10 Y=152 Z=0
    g13: LineSegment [constr] StartX=-7.3 StartY=152 StartZ=0 EndX=-12.7 EndY=152 EndZ=0
    g14: LineSegment StartX=-5.42426 StartY=149.7 StartZ=0 EndX=0 EndY=149.7 EndZ=0
  constraints (42):
    c: Coincident(g0,g1)
    c: Coincident(g14,g2)
    c: Coincident(g2,g3)
    c: Coincident(g3,g0)
    c: Vertical(g0)
    c: Vertical(g2)
    c: Horizontal(g1)
    c: Horizontal(g3)
    c: PointOnObject(g14,g-2)
    c: DistanceX(g3,g3) = 24
    c: DistanceY(g2) = 170
    c: DistanceY(g2,g2) = 20.3
    c: Coincident(g4,g5)
    c: Coincident(g5,g6)
    c: Coincident(g6,g7)
    c: Coincident(g7,g4)
    c: Vertical(g4)
    c: Vertical(g6)
    c: Horizontal(g5)
    c: Horizontal(g7)
    c: PointOnObject(g4,g3)
    c: PointOnObject(g5,g2)
    c: Equal(g4,g5)
    c: DistanceY(g4,g4) = 20
    c: Symmetric(g5,g5,g8)
    c: Coincident(g9,g10)
    c: Horizontal(g10)
    c: Coincident(g10,g11)
    c: PointOnObject(g11,g14)
    c: Perpendicular(g11,g9)
    c: Angle(g11) = -0.785398
    c: Symmetric(g10,g10,g12)
    c: Vertical(g12,g8)
    c: DistanceY(g8,g10) = 2
    c: Horizontal(g13)
    c: Symmetric(g13,g13,g12)
    c: DistanceX(g13,g13) = 5.4
    c: Distance(g13,g9) = 0.3
    c: Coincident(g1,g9)
    c: PointOnObject(g14,g11)
    c: Horizontal(g14)
    c: Horizontal(g11,g1)
FEATURE [PartDesign::Pocket] Pocket284
  BaseFeature = -> Pocket283
  Direction = (0,0,-1)
  Length = 5
  Length2 = 5
  Midplane = true
  Placement = pos=(0,0,0) rot=(1,1,1;2.0944rad)
  Profile = -> Sketch410
  ReferenceAxis = -> Sketch410 [N_Axis]
  Suppressed = false
  Type = 1
FEATURE [Sketcher::SketchObject] Sketch417
  ArcFitTolerance = 1e-06
  AttachmentOffset = pos=(0,0,3) rot=(0,0,1;0rad)
  AttachmentSupport = -> [YZ_Plane268]
  FullyConstrained = true
  MakeInternals = false
  MapMode = 5
  Placement = pos=(3,0,0) rot=(0.57735,0.57735,0.57735;2.0944rad)
  expr: Constraints[4] = Spreadsheet.side_length / 2
  sketch-geometry (4):
    g0: Circle CenterX=20 CenterY=10 CenterZ=0 NormalX=0 NormalY=0 NormalZ=1 AngleXU=0 Radius=5
    g1: Circle CenterX=110 CenterY=10 CenterZ=0 NormalX=0 NormalY=0 NormalZ=1 AngleXU=0 Radius=5
    g2: GeomPoint X=170 Y=0 Z=0
    g3: GeomPoint X=130 Y=0 Z=0
  constraints (10):
    c: Horizontal(g0,g1)
    c: DistanceY(g0) = 10
    c: DistanceX(g0) = 20
    c: PointOnObject(g2,g-1)
    c: DistanceX(g2) = 170
    c: PointOnObject(g3,g-1)
    c: DistanceX(g3,g2) = 40
    c: DistanceX(g1,g3) = 20
    c: Equal(g0,g1)
    c: Diameter(g1) = 10
FEATURE [PartDesign::Pocket] Pocket290
  BaseFeature = -> Pocket284
  Direction = (-1,0,0)
  Length = 5
  Length2 = 5
  Placement = pos=(0,0,0) rot=(1,1,1;2.0944rad)
  Profile = -> Sketch417
  ReferenceAxis = -> Sketch417 [N_Axis]
  Reversed = true
  Suppressed = false
  Type = 1
FEATURE [Sketcher::SketchObject] Sketch418
  ArcFitTolerance = 1e-06
  AttachmentOffset = pos=(0,0,2.7) rot=(0,0,1;0rad)
  AttachmentSupport = -> [YZ_Plane268]
  FullyConstrained = true
  MakeInternals = false
  MapMode = 5
  Placement = pos=(2.7,0,0) rot=(0.57735,0.57735,0.57735;2.0944rad)
  expr: Constraints[4] = Spreadsheet.side_length / 2
  sketch-geometry (4):
    g0: Circle CenterX=20 CenterY=10 CenterZ=0 NormalX=0 NormalY=0 NormalZ=1 AngleXU=0 Radius=2.75
    g1: Circle CenterX=110 CenterY=10 CenterZ=0 NormalX=0 NormalY=0 NormalZ=1 AngleXU=0 Radius=2.75
    g2: GeomPoint X=170 Y=0 Z=0
    g3: GeomPoint X=130 Y=0 Z=0
  constraints (10):
    c: Horizontal(g0,g1)
    c: DistanceY(g0) = 10
    c: DistanceX(g0) = 20
    c: PointOnObject(g2,g-1)
    c: DistanceX(g2) = 170
    c: PointOnObject(g3,g-1)
    c: DistanceX(g3,g2) = 40
    c: DistanceX(g1,g3) = 20
    c: Equal(g0,g1)
    c: Diameter(g1) = 5.5
FEATURE [PartDesign::Pocket] Pocket291
  BaseFeature = -> Pocket290
  Direction = (-1,0,0)
  Length = 5
  Length2 = 5
  Placement = pos=(0,0,0) rot=(1,1,1;2.0944rad)
  Profile = -> Sketch418
  ReferenceAxis = -> Sketch418 [N_Axis]
  Suppressed = false
  Type = 1
FEATURE [Sketcher::SketchObject] Sketch419
  ArcFitTolerance = 1e-06
  AttachmentSupport = -> [YZ_Plane268]
  FullyConstrained = true
  MakeInternals = false
  MapMode = 5
  Placement = pos=(0,0,0) rot=(0.57735,0.57735,0.57735;2.0944rad)
  expr: Constraints[4] = Spreadsheet.side_length / 2
  sketch-geometry (12):
    g0: Circle [constr] CenterX=20 CenterY=10 CenterZ=0 NormalX=0 NormalY=0 NormalZ=1 AngleXU=0 Radius=5
    g1: Circle [constr] CenterX=110 CenterY=10 CenterZ=0 NormalX=0 NormalY=0 NormalZ=1 AngleXU=0 Radius=5
    g2: GeomPoint X=170 Y=0 Z=0
    g3: GeomPoint X=130 Y=0 Z=0
    g4: LineSegment StartX=12 StartY=18 StartZ=0 EndX=12 EndY=2 EndZ=0
    g5: LineSegment StartX=12 StartY=2 StartZ=0 EndX=28 EndY=2 EndZ=0
    g6: LineSegment StartX=28 StartY=2 StartZ=0 EndX=28 EndY=18 EndZ=0
    g7: LineSegment StartX=28 StartY=18 StartZ=0 EndX=12 EndY=18 EndZ=0
    g8: LineSegment StartX=102 StartY=18 StartZ=0 EndX=102 EndY=2 EndZ=0
    g9: LineSegment StartX=102 StartY=2 StartZ=0 EndX=118 EndY=2 EndZ=0
    g10: LineSegment StartX=118 StartY=2 StartZ=0 EndX=118 EndY=18 EndZ=0
    g11: LineSegment StartX=118 StartY=18 StartZ=0 EndX=102 EndY=18 EndZ=0
  constraints (32):
    c: Horizontal(g0,g1)
    c: DistanceY(g0) = 10
    c: DistanceX(g0) = 20
    c: PointOnObject(g2,g-1)
    c: DistanceX(g2) = 170
    c: PointOnObject(g3,g-1)
    c: DistanceX(g3,g2) = 40
    c: DistanceX(g1,g3) = 20
    c: Equal(g0,g1)
    c: Diameter(g1) = 10
    c: Coincident(g4,g5)
    c: Coincident(g5,g6)
    c: Coincident(g6,g7)
    c: Coincident(g7,g4)
    c: Vertical(g4)
    c: Vertical(g6)
    c: Horizontal(g5)
    c: Horizontal(g7)
    c: Coincident(g8,g9)
    c: Coincident(g9,g10)
    c: Coincident(g10,g11)
    c: Coincident(g11,g8)
    c: Vertical(g8)
    c: Vertical(g10)
    c: Horizontal(g9)
    c: Horizontal(g11)
    c: Equal(g10,g11)
    c: Equal(g11,g6)
    c: Equal(g6,g7)
    c: DistanceY(g6,g6) = 16
    c: Symmetric(g5,g4,g0)
    c: Symmetric(g10,g8,g1)
FEATURE [PartDesign::Pocket] Pocket292
  BaseFeature = -> Pocket291
  Direction = (-1,0,0)
  Length = 5
  Length2 = 5
  Placement = pos=(0,0,0) rot=(1,1,1;2.0944rad)
  Profile = -> Sketch419
  ReferenceAxis = -> Sketch419 [N_Axis]
  Refine = true
  Suppressed = false
  Type = 1
FEATURE [Sketcher::SketchObject] Sketch464
  ArcFitTolerance = 1e-06
  AttachmentSupport = -> [YZ_Plane268]
  FullyConstrained = true
  MakeInternals = false
  MapMode = 5
  Placement = pos=(0,0,0) rot=(0.57735,0.57735,0.57735;2.0944rad)
  expr: Constraints[1] = Spreadsheet.side_length / 2
  sketch-geometry (8):
    g0: GeomPoint X=170 Y=0 Z=0
    g1: LineSegment StartX=170 StartY=0 StartZ=0 EndX=170 EndY=40.5 EndZ=0
    g2: LineSegment [constr] StartX=170 StartY=40.5 StartZ=0 EndX=129.5 EndY=40.5 EndZ=0
    g3: LineSegment [constr] StartX=129.5 StartY=40.5 StartZ=0 EndX=129.5 EndY=0 EndZ=0
    g4: LineSegment StartX=129.5 StartY=0 StartZ=0 EndX=170 EndY=0 EndZ=0
    g5: LineSegment StartX=170 StartY=40.5 StartZ=0 EndX=137.5 EndY=40.5 EndZ=0
    g6: LineSegment StartX=129.5 StartY=0 StartZ=0 EndX=129.5 EndY=32.5 EndZ=0
    g7: ArcOfCircle CenterX=137.5 CenterY=32.5 CenterZ=0 NormalX=0 NormalY=0 NormalZ=1 AngleXU=0 Radius=8 StartAngle=1.5708 EndAngle=3.14159
  constraints (20):
    c: PointOnObject(g0,g-1)
    c: DistanceX(g0) = 170
    c: Coincident(g1,g2)
    c: Coincident(g2,g3)
    c: Coincident(g3,g4)
    c: Coincident(g4,g1)
    c: Vertical(g1)
    c: Vertical(g3)
    c: Horizontal(g2)
    c: Horizontal(g4)
    c: Coincident(g1,g0)
    c: Equal(g2,g3)
    c: DistanceX(g2,g2) = 40.5
    c: Coincident(g1,g5)
    c: PointOnObject(g5,g2)
    c: Coincident(g3,g6)
    c: PointOnObject(g6,g3)
    c: Tangent(g7,g5) = -1.5708
    c: Tangent(g7,g6) = 1.5708
    c: Radius(g7) = 8
FEATURE [PartDesign::Pocket] Pocket328
  BaseFeature = -> Pocket292
  Direction = (-1,0,0)
  Length = 5
  Length2 = 5
  Placement = pos=(0,0,0) rot=(1,1,1;2.0944rad)
  Profile = -> Sketch464
  ReferenceAxis = -> Sketch464 [N_Axis]
  Refine = true
  Suppressed = false
  Type = 1
FEATURE [Sketcher::SketchObject] Sketch479
  ArcFitTolerance = 1e-06
  AttachmentSupport = -> [YZ_Plane268]
  FullyConstrained = true
  MakeInternals = false
  MapMode = 5
  Placement = pos=(0,0,0) rot=(0.57735,0.57735,0.57735;2.0944rad)
  sketch-geometry (4):
    g0: LineSegment StartX=0 StartY=55 StartZ=0 EndX=154 EndY=55 EndZ=0
    g1: LineSegment StartX=154 StartY=55 StartZ=0 EndX=154 EndY=63 EndZ=0
    g2: LineSegment StartX=154 StartY=63 StartZ=0 EndX=0 EndY=63 EndZ=0
    g3: LineSegment StartX=0 StartY=63 StartZ=0 EndX=0 EndY=55 EndZ=0
  constraints (12):
    c: Coincident(g0,g1)
    c: Coincident(g1,g2)
    c: Coincident(g2,g3)
    c: Coincident(g3,g0)
    c: Horizontal(g0)
    c: Horizontal(g2)
    c: Vertical(g1)
    c: Vertical(g3)
    c: PointOnObject(g0,g-2)
    c: DistanceX(g0) = 154
    c: DistanceY(g0) = 55
    c: DistanceY(g1,g1) = 8
FEATURE [PartDesign::Pad] Pad106
  BaseFeature = -> Pocket328
  Direction = (1,0,0)
  Length = 6
  Length2 = -3.2
  Placement = pos=(0,0,0) rot=(1,1,1;2.0944rad)
  Profile = -> Sketch479
  ReferenceAxis = -> Sketch479 [N_Axis]
  Refine = true
  Suppressed = false
  Type = 4
FEATURE [PartDesign::Body] Body133  label="skirt-right-back-drv"
  AllowCompound = false
  Group = -> [Sketch408,Pad089,Sketch409,Pocket283,Sketch410,Pocket284,Sketch417,Pocket290,Sketch418,Pocket291,Sketch419,Pocket292,Sketch464,Pocket328,Sketch479,Pad106]
  Origin = -> Origin269
  Tip = -> Pad106
COMPONENT P8 — recipe-attached ("skirt-front-right-drv", modeled in this document).
Construction recipe (the document's own serialized feature program — sketch geometry with constraints, then the solid features built on it; lengths are millimeters unless a unit is written):

FEATURE [Sketcher::SketchObject] Sketch411
  ArcFitTolerance = 1e-06
  AttachmentSupport = -> [XZ_Plane270]
  FullyConstrained = true
  MakeInternals = false
  MapMode = 5
  Placement = pos=(0,0,0) rot=(1,0,0;1.5708rad)
  expr: Constraints[20] = Spreadsheet.side_length / 2
  sketch-geometry (9):
    g0: LineSegment StartX=0 StartY=0 StartZ=0 EndX=0 EndY=55 EndZ=0
    g1: LineSegment StartX=0 StartY=55 StartZ=0 EndX=154 EndY=55 EndZ=0
    g2: LineSegment StartX=154 StartY=55 StartZ=0 EndX=154 EndY=36.5 EndZ=0
    g3: LineSegment StartX=154 StartY=36.5 StartZ=0 EndX=137.5 EndY=36.5 EndZ=0
    g4: LineSegment StartX=133.5 StartY=32.5 StartZ=0 EndX=133.5 EndY=0 EndZ=0
    g5: LineSegment StartX=133.5 StartY=0 StartZ=0 EndX=0 EndY=0 EndZ=0
    g6: ArcOfCircle CenterX=137.5 CenterY=32.5 CenterZ=0 NormalX=0 NormalY=0 NormalZ=1 AngleXU=0 Radius=4 StartAngle=1.5708 EndAngle=3.14159
    g7: GeomPoint [constr] X=133.5 Y=36.5 Z=0
    g8: GeomPoint [constr] X=170 Y=0 Z=0
  constraints (23):
    c: Coincident(g-1,g0)
    c: PointOnObject(g0,g-2)
    c: Coincident(g0,g1)
    c: Horizontal(g1)
    c: Coincident(g1,g2)
    c: Vertical(g2)
    c: Coincident(g2,g3)
    c: Horizontal(g3)
    c: Coincident(g4,g5)
    c: Coincident(g5,g0)
    c: Horizontal(g5)
    c: Vertical(g4)
    c: PointOnObject(g7,g3)
    c: PointOnObject(g7,g4)
    c: Tangent(g3,g6) = -1.5708
    c: Tangent(g4,g6) = -1.5708
    c: Radius(g6) = 4
    c: DistanceY(g2) = 36.5
    c: DistanceY(g1) = 55
    c: PointOnObject(g8,g-1)
    c: DistanceX(g8) = 170
    c: DistanceX(g4,g8) = 36.5
    c: DistanceX(g2,g8) = 16
FEATURE [PartDesign::Pad] Pad090
  Direction = (0,-1,2e-16)
  Length = 6
  Length2 = 4
  Placement = pos=(0,0,0) rot=(1,0,0;1.5708rad)
  Profile = -> Sketch411
  ReferenceAxis = -> Sketch411 [N_Axis]
  Suppressed = false
  Type = 4
FEATURE [Sketcher::SketchObject] Sketch412
  ArcFitTolerance = 1e-06
  AttachmentSupport = -> [YZ_Plane270]
  FullyConstrained = true
  MakeInternals = false
  MapMode = 5
  Placement = pos=(0,0,0) rot=(0.57735,0.57735,0.57735;2.0944rad)
  sketch-geometry (16):
    g0: LineSegment [constr] StartX=0 StartY=20 StartZ=0 EndX=0 EndY=0 EndZ=0
    g1: LineSegment StartX=0 StartY=0 StartZ=0 EndX=20 EndY=0 EndZ=0
    g2: LineSegment StartX=20 StartY=0 StartZ=0 EndX=20 EndY=20 EndZ=0
    g3: LineSegment StartX=20 StartY=20 StartZ=0 EndX=0 EndY=20 EndZ=0
    g4: LineSegment StartX=0 StartY=20 StartZ=0 EndX=0 EndY=14.2757 EndZ=0
    g5: LineSegment StartX=0 StartY=14.2757 StartZ=0 EndX=2 EndY=12.2757 EndZ=0
    g6: LineSegment StartX=2 StartY=12.2757 StartZ=0 EndX=2 EndY=7.72426 EndZ=0
    g7: LineSegment StartX=2 StartY=7.72426 StartZ=0 EndX=0 EndY=5.72426 EndZ=0
    g8: LineSegment StartX=0 StartY=5.72426 StartZ=0 EndX=0 EndY=0 EndZ=0
    g9: GeomPoint X=0 Y=10 Z=0
    g10: GeomPoint X=2 Y=10 Z=0
    g11: LineSegment [constr] StartX=2 StartY=12.7 StartZ=0 EndX=2 EndY=7.3 EndZ=0
    g12: LineSegment StartX=0 StartY=55 StartZ=0 EndX=0 EndY=50 EndZ=0
    g13: LineSegment StartX=0 StartY=50 StartZ=0 EndX=4 EndY=50 EndZ=0
    g14: LineSegment StartX=4 StartY=50 StartZ=0 EndX=4 EndY=55 EndZ=0
    g15: LineSegment StartX=4 StartY=55 StartZ=0 EndX=0 EndY=55 EndZ=0
  constraints (43):
    c: Coincident(g0,g1)
    c: Coincident(g1,g2)
    c: Coincident(g2,g3)
    c: Coincident(g3,g0)
    c: Vertical(g0)
    c: Vertical(g2)
    c: Horizontal(g1)
    c: Horizontal(g3)
    c: PointOnObject(g0,g-2)
    c: PointOnObject(g1,g-1)
    c: Equal(g2,g3)
    c: DistanceX(g3,g3) = 20
    c: Coincident(g0,g4)
    c: PointOnObject(g4,g0)
    c: Coincident(g4,g5)
    c: Coincident(g5,g6)
    c: Vertical(g6)
    c: Coincident(g6,g7)
    c: PointOnObject(g7,g0)
    c: Coincident(g7,g8)
    c: Coincident(g8,g0)
    c: Perpendicular(g5,g7)
    c: Symmetric(g0,g0,g9)
    c: Symmetric(g6,g6,g10)
    c: Horizontal(g10,g9)
    c: Angle(g5) = -0.785398
    c: DistanceX(g5,g5) = 2
    c: Vertical(g11)
    c: Symmetric(g11,g11,g10)
    c: DistanceY(g11,g11) = 5.4
    c: Distance(g11,g7) = 0.3
    c: Coincident(g12,g13)
    c: Coincident(g13,g14)
    c: Coincident(g14,g15)
    c: Coincident(g15,g12)
    c: Vertical(g12)
    c: Vertical(g14)
    c: Horizontal(g13)
    c: Horizontal(g15)
    c: PointOnObject(g12,g-2)
    c: DistanceY(g12) = 55
    c: DistanceY(g12) = 50
    c: DistanceX(g13,g13) = 4
FEATURE [PartDesign::Pocket] Pocket285
  BaseFeature = -> Pad090
  Direction = (-1,0,0)
  Length = 5
  Length2 = 5
  Midplane = true
  Placement = pos=(0,0,0) rot=(1,0,0;1.5708rad)
  Profile = -> Sketch412
  ReferenceAxis = -> Sketch412 [N_Axis]
  Suppressed = false
  Type = 1
FEATURE [Sketcher::SketchObject] Sketch413
  ArcFitTolerance = 1e-06
  AttachmentSupport = -> [XY_Plane270]
  FullyConstrained = true
  MakeInternals = false
  MapMode = 5
  expr: Constraints[9] = Spreadsheet.side_length / 2
  sketch-geometry (4):
    g0: LineSegment StartX=149.7 StartY=20 StartZ=0 EndX=149.7 EndY=0 EndZ=0
    g1: LineSegment StartX=149.7 StartY=0 StartZ=0 EndX=170 EndY=0 EndZ=0
    g2: LineSegment StartX=170 StartY=0 StartZ=0 EndX=170 EndY=20 EndZ=0
    g3: LineSegment StartX=170 StartY=20 StartZ=0 EndX=149.7 EndY=20 EndZ=0
  constraints (12):
    c: Coincident(g0,g1)
    c: Coincident(g1,g2)
    c: Coincident(g2,g3)
    c: Coincident(g3,g0)
    c: Vertical(g0)
    c: Vertical(g2)
    c: Horizontal(g1)
    c: Horizontal(g3)
    c: PointOnObject(g1,g-1)
    c: DistanceX(g1) = 170
    c: DistanceX(g3,g3) = 20.3
    c: DistanceY(g2,g2) = 20
FEATURE [PartDesign::Pocket] Pocket286
  BaseFeature = -> Pocket285
  Direction = (0,0,-1)
  Length = 5
  Length2 = 5
  Midplane = true
  Placement = pos=(0,0,0) rot=(1,0,0;1.5708rad)
  Profile = -> Sketch413
  ReferenceAxis = -> Sketch413 [N_Axis]
  Suppressed = false
  Type = 1
FEATURE [Sketcher::SketchObject] Sketch421
  ArcFitTolerance = 1e-06
  AttachmentOffset = pos=(0,0,2.7) rot=(0,0,1;0rad)
  AttachmentSupport = -> [XZ_Plane270]
  FullyConstrained = true
  MakeInternals = false
  MapMode = 5
  Placement = pos=(0,-2.7,6e-16) rot=(1,0,0;1.5708rad)
  expr: Constraints[1] = Spreadsheet.side_length / 2
  sketch-geometry (3):
    g0: Circle CenterX=20 CenterY=10 CenterZ=0 NormalX=0 NormalY=0 NormalZ=1 AngleXU=0 Radius=2.75
    g1: Circle CenterX=110 CenterY=10 CenterZ=0 NormalX=0 NormalY=0 NormalZ=1 AngleXU=0 Radius=2.75
    g2: GeomPoint X=170 Y=0 Z=0
  constraints (8):
    c: PointOnObject(g2,g-1)
    c: DistanceX(g2) = 170
    c: DistanceX(g1,g2) = 60
    c: DistanceX(g0) = 20
    c: Equal(g0,g1)
    c: Horizontal(g1,g0)
    c: Diameter(g0) = 5.5
    c: DistanceY(g0) = 10
FEATURE [PartDesign::Pocket] Pocket294
  BaseFeature = -> Pocket286
  Direction = (0,1,-2e-16)
  Length = 5
  Length2 = 5
  Placement = pos=(0,0,0) rot=(1,0,0;1.5708rad)
  Profile = -> Sketch421
  ReferenceAxis = -> Sketch421 [N_Axis]
  Suppressed = false
  Type = 1
FEATURE [Sketcher::SketchObject] Sketch422
  ArcFitTolerance = 1e-06
  AttachmentOffset = pos=(0,0,3) rot=(0,0,1;0rad)
  AttachmentSupport = -> [XZ_Plane270]
  FullyConstrained = true
  MakeInternals = false
  MapMode = 5
  Placement = pos=(0,-3,7e-16) rot=(1,0,0;1.5708rad)
  expr: Constraints[1] = Spreadsheet.side_length / 2
  sketch-geometry (3):
    g0: Circle CenterX=20 CenterY=10 CenterZ=0 NormalX=0 NormalY=0 NormalZ=1 AngleXU=0 Radius=5
    g1: Circle CenterX=110 CenterY=10 CenterZ=0 NormalX=0 NormalY=0 NormalZ=1 AngleXU=0 Radius=5
    g2: GeomPoint X=170 Y=0 Z=0
  constraints (8):
    c: PointOnObject(g2,g-1)
    c: DistanceX(g2) = 170
    c: DistanceX(g1,g2) = 60
    c: DistanceX(g0) = 20
    c: Equal(g0,g1)
    c: Horizontal(g1,g0)
    c: Diameter(g0) = 10
    c: DistanceY(g0) = 10
FEATURE [PartDesign::Pocket] Pocket295
  BaseFeature = -> Pocket294
  Direction = (0,1,-2e-16)
  Length = 5
  Length2 = 5
  Placement = pos=(0,0,0) rot=(1,0,0;1.5708rad)
  Profile = -> Sketch422
  ReferenceAxis = -> Sketch422 [N_Axis]
  Reversed = true
  Suppressed = false
  Type = 1
FEATURE [Sketcher::SketchObject] Sketch423
  ArcFitTolerance = 1e-06
  AttachmentSupport = -> [XZ_Plane270]
  FullyConstrained = true
  MakeInternals = false
  MapMode = 5
  Placement = pos=(0,0,0) rot=(1,0,0;1.5708rad)
  expr: Constraints[1] = Spreadsheet.side_length / 2
  sketch-geometry (11):
    g0: Circle [constr] CenterX=20 CenterY=10 CenterZ=0 NormalX=0 NormalY=0 NormalZ=1 AngleXU=0 Radius=2.75
    g1: Circle [constr] CenterX=110 CenterY=10 CenterZ=0 NormalX=0 NormalY=0 NormalZ=1 AngleXU=0 Radius=2.75
    g2: GeomPoint X=170 Y=0 Z=0
    g3: LineSegment StartX=12 StartY=18 StartZ=0 EndX=12 EndY=2 EndZ=0
    g4: LineSegment StartX=12 StartY=2 StartZ=0 EndX=28 EndY=2 EndZ=0
    g5: LineSegment StartX=28 StartY=2 StartZ=0 EndX=28 EndY=18 EndZ=0
    g6: LineSegment StartX=28 StartY=18 StartZ=0 EndX=12 EndY=18 EndZ=0
    g7: LineSegment StartX=102 StartY=18 StartZ=0 EndX=102 EndY=2 EndZ=0
    g8: LineSegment StartX=102 StartY=2 StartZ=0 EndX=118 EndY=2 EndZ=0
    g9: LineSegment StartX=118 StartY=2 StartZ=0 EndX=118 EndY=18 EndZ=0
    g10: LineSegment StartX=118 StartY=18 StartZ=0 EndX=102 EndY=18 EndZ=0
  constraints (30):
    c: PointOnObject(g2,g-1)
    c: DistanceX(g2) = 170
    c: DistanceX(g1,g2) = 60
    c: DistanceX(g0) = 20
    c: Equal(g0,g1)
    c: Horizontal(g1,g0)
    c: Diameter(g0) = 5.5
    c: DistanceY(g0) = 10
    c: Coincident(g3,g4)
    c: Coincident(g4,g5)
    c: Coincident(g5,g6)
    c: Coincident(g6,g3)
    c: Vertical(g3)
    c: Vertical(g5)
    c: Horizontal(g4)
    c: Horizontal(g6)
    c: Coincident(g7,g8)
    c: Coincident(g8,g9)
    c: Coincident(g9,g10)
    c: Coincident(g10,g7)
    c: Vertical(g7)
    c: Vertical(g9)
    c: Horizontal(g8)
    c: Horizontal(g10)
    c: Equal(g9,g10)
    c: Equal(g10,g6)
    c: Equal(g6,g3)
    c: DistanceX(g6,g6) = 16
    c: Symmetric(g5,g3,g0)
    c: Symmetric(g9,g7,g1)
FEATURE [PartDesign::Pocket] Pocket296
  BaseFeature = -> Pocket295
  Direction = (0,1,-2e-16)
  Length = 5
  Length2 = 5
  Placement = pos=(0,0,0) rot=(1,0,0;1.5708rad)
  Profile = -> Sketch423
  ReferenceAxis = -> Sketch423 [N_Axis]
  Refine = true
  Suppressed = false
  Type = 1
FEATURE [Sketcher::SketchObject] Sketch465
  ArcFitTolerance = 1e-06
  AttachmentSupport = -> [XZ_Plane270]
  FullyConstrained = true
  MakeInternals = false
  MapMode = 5
  Placement = pos=(0,0,0) rot=(1,0,0;1.5708rad)
  expr: Constraints[1] = Spreadsheet.side_length / 2
  sketch-geometry (6):
    g0: GeomPoint X=170 Y=0 Z=0
    g1: LineSegment StartX=170 StartY=0 StartZ=0 EndX=170 EndY=40.5 EndZ=0
    g2: LineSegment StartX=129.5 StartY=0 StartZ=0 EndX=170 EndY=0 EndZ=0
    g3: LineSegment StartX=170 StartY=40.5 StartZ=0 EndX=137.5 EndY=40.5 EndZ=0
    g4: LineSegment StartX=129.5 StartY=0 StartZ=0 EndX=129.5 EndY=32.5 EndZ=0
    g5: ArcOfCircle CenterX=137.5 CenterY=32.5 CenterZ=0 NormalX=0 NormalY=0 NormalZ=1 AngleXU=0 Radius=8 StartAngle=1.5708 EndAngle=3.14159
  constraints (15):
    c: PointOnObject(g0,g-1)
    c: DistanceX(g0) = 170
    c: Coincident(g2,g1)
    c: Vertical(g1)
    c: Horizontal(g2)
    c: Coincident(g1,g0)
    c: DistanceY(g1,g1) = 40.5
    c: Coincident(g1,g3)
    c: Radius(g5) = 8
    c: Tangent(g5,g4) = 1.5708
    c: Tangent(g5,g3) = -1.5708
    c: Horizontal(g3)
    c: Vertical(g4)
    c: Equal(g2,g1)
    c: Coincident(g2,g4)
FEATURE [PartDesign::Pocket] Pocket329
  BaseFeature = -> Pocket296
  Direction = (0,1,-2e-16)
  Length = 5
  Length2 = 5
  Placement = pos=(0,0,0) rot=(1,0,0;1.5708rad)
  Profile = -> Sketch465
  ReferenceAxis = -> Sketch465 [N_Axis]
  Refine = true
  Suppressed = false
  Type = 1
FEATURE [PartDesign::Body] Body134  label="skirt-front-right-drv"
  AllowCompound = false
  Group = -> [Sketch411,Pad090,Sketch412,Pocket285,Sketch413,Pocket286,Sketch421,Pocket294,Sketch422,Pocket295,Sketch423,Pocket296,Sketch465,Pocket329]
  Origin = -> Origin271
  Tip = -> Pocket329
COMPONENT P9 — recipe-attached ("hinge-stat-drv", modeled in this document).
Construction recipe (the document's own serialized feature program — sketch geometry with constraints, then the solid features built on it; lengths are millimeters unless a unit is written):

FEATURE [Sketcher::SketchObject] Sketch431
  ArcFitTolerance = 1e-06
  AttachmentSupport = -> [XZ_Plane283]
  FullyConstrained = true
  MakeInternals = false
  MapMode = 5
  Placement = pos=(0,0,0) rot=(1,0,0;1.5708rad)
  sketch-geometry (10):
    g0: LineSegment StartX=-11 StartY=8 StartZ=0 EndX=-11 EndY=-8 EndZ=0
    g1: LineSegment StartX=-9 StartY=-10 StartZ=0 EndX=5 EndY=-10 EndZ=0
    g2: LineSegment StartX=5 StartY=-10 StartZ=0 EndX=5 EndY=10 EndZ=0
    g3: LineSegment StartX=5 StartY=10 StartZ=0 EndX=-9 EndY=10 EndZ=0
    g4: ArcOfCircle CenterX=-9 CenterY=8 CenterZ=0 NormalX=0 NormalY=0 NormalZ=1 AngleXU=0 Radius=2 StartAngle=1.5708 EndAngle=3.14159
    g5: GeomPoint [constr] X=-11 Y=10 Z=0
    g6: GeomPoint [constr] X=5 Y=10 Z=0
    g7: GeomPoint [constr] X=5 Y=-10 Z=0
    g8: ArcOfCircle CenterX=-9 CenterY=-8 CenterZ=0 NormalX=0 NormalY=0 NormalZ=1 AngleXU=0 Radius=2 StartAngle=3.14159 EndAngle=4.71239
    g9: GeomPoint [constr] X=-11 Y=-10 Z=0
  constraints (21):
    c: Vertical(g2)
    c: Horizontal(g1)
    c: Horizontal(g3)
    c: Symmetric(g5,g9,g-1)
    c: DistanceX(g5) = -11
    c: PointOnObject(g5,g0)
    c: PointOnObject(g5,g3)
    c: Tangent(g0,g4) = -1.5708
    c: Tangent(g3,g4) = -1.5708
    c: PointOnObject(g9,g0)
    c: PointOnObject(g9,g1)
    c: Tangent(g0,g8) = -1.5708
    c: Tangent(g1,g8) = -1.5708
    c: Equal(g8,g4)
    c: Radius(g8) = 2
    c: DistanceX(g6) = 5
    c: DistanceY(g9,g5) = 20
    c: Coincident(g3,g6)
    c: Coincident(g3,g2)
    c: Coincident(g2,g7)
    c: Coincident(g2,g1)
FEATURE [PartDesign::Pad] Pad094
  Direction = (0,-1,2e-16)
  Length = 8
  Length2 = 10
  Placement = pos=(0,0,0) rot=(1,0,0;1.5708rad)
  Profile = -> Sketch431
  ReferenceAxis = -> Sketch431 [N_Axis]
  Suppressed = false
  Type = 0
FEATURE [Sketcher::SketchObject] Sketch432
  ArcFitTolerance = 1e-06
  AttachmentOffset = pos=(0,0,4) rot=(0,0,1;0rad)
  AttachmentSupport = -> [XZ_Plane283]
  FullyConstrained = true
  MakeInternals = false
  MapMode = 5
  Placement = pos=(0,-4,9e-16) rot=(1,0,0;1.5708rad)
  sketch-geometry (5):
    g0: Circle [constr] CenterX=0 CenterY=0 CenterZ=0 NormalX=0 NormalY=0 NormalZ=1 AngleXU=0 Radius=5
    g1: LineSegment StartX=3e-16 StartY=5 StartZ=0 EndX=5 EndY=5 EndZ=0
    g2: LineSegment StartX=-9e-16 StartY=-5 StartZ=0 EndX=5 EndY=-5 EndZ=0
    g3: LineSegment StartX=5 StartY=-5 StartZ=0 EndX=5 EndY=5 EndZ=0
    g4: ArcOfCircle CenterX=0 CenterY=0 CenterZ=0 NormalX=0 NormalY=0 NormalZ=1 AngleXU=0 Radius=5 StartAngle=1.5708 EndAngle=4.71239
  constraints (12):
    c: Coincident(g0,g-1)
    c: Diameter(g0) = 10
    c: Tangent(g1,g0) = 1.5708
    c: Horizontal(g1)
    c: Coincident(g3,g2)
    c: Coincident(g3,g1)
    c: Vertical(g3)
    c: DistanceX(g2) = 5
    c: Tangent(g2,g0) = -1.5708
    c: Coincident(g4,g1)
    c: Horizontal(g2)
    c: Tangent(g4,g2) = -1.5708
FEATURE [PartDesign::Pocket] Pocket301
  BaseFeature = -> Pad094
  Direction = (0,1,-2e-16)
  Length = 5
  Length2 = 5
  Placement = pos=(0,0,0) rot=(1,0,0;1.5708rad)
  Profile = -> Sketch432
  ReferenceAxis = -> Sketch432 [N_Axis]
  Reversed = true
  Suppressed = false
  Type = 1
FEATURE [Sketcher::SketchObject] Sketch433
  ArcFitTolerance = 1e-06
  AttachmentSupport = -> [XY_Plane283]
  FullyConstrained = true
  MakeInternals = false
  MapMode = 5
  sketch-geometry (1):
    g0: Circle CenterX=-7 CenterY=-4 CenterZ=0 NormalX=0 NormalY=0 NormalZ=1 AngleXU=0 Radius=1.7
  constraints (3):
    c: Diameter(g0) = 3.4
    c: DistanceY(g0) = -4
    c: DistanceX(g0) = -7
FEATURE [PartDesign::Pocket] Pocket302
  BaseFeature = -> Pocket301
  Direction = (0,0,-1)
  Length = 5
  Length2 = 5
  Midplane = true
  Placement = pos=(0,0,0) rot=(1,0,0;1.5708rad)
  Profile = -> Sketch433
  ReferenceAxis = -> Sketch433 [N_Axis]
  Suppressed = false
  Type = 1
FEATURE [Sketcher::SketchObject] Sketch434
  ArcFitTolerance = 1e-06
  AttachmentSupport = -> [XY_Plane283]
  FullyConstrained = true
  MakeInternals = false
  MapMode = 5
  sketch-geometry (5):
    g0: LineSegment StartX=-4.27574 StartY=0 StartZ=0 EndX=-2.27574 EndY=2 EndZ=0
    g1: LineSegment StartX=-2.27574 StartY=2 StartZ=0 EndX=2.27574 EndY=2 EndZ=0
    g2: LineSegment StartX=2.27574 StartY=2 StartZ=0 EndX=4.27574 EndY=0 EndZ=0
    g3: LineSegment StartX=4.27574 StartY=0 StartZ=0 EndX=-4.27574 EndY=0 EndZ=0
    g4: LineSegment [constr] StartX=-2.7 StartY=2 StartZ=0 EndX=2.7 EndY=2 EndZ=0
  constraints (14):
    c: PointOnObject(g0,g-1)
    c: Coincident(g0,g1)
    c: Coincident(g1,g2)
    c: PointOnObject(g2,g-1)
    c: Coincident(g2,g3)
    c: Coincident(g3,g0)
    c: Symmetric(g1,g0,g-2)
    c: Perpendicular(g2,g0)
    c: Angle(g2) = -0.785398
    c: DistanceY(g2,g2) = 2
    c: Symmetric(g4,g4,g-2)
    c: PointOnObject(g0,g4)
    c: DistanceX(g4,g4) = 5.4
    c: Distance(g4,g0) = 0.3
FEATURE [PartDesign::Pad] Pad095
  BaseFeature = -> Pocket302
  Direction = (0,0,1)
  Length = 20
  Length2 = 10
  Midplane = true
  Placement = pos=(0,0,0) rot=(1,0,0;1.5708rad)
  Profile = -> Sketch434
  ReferenceAxis = -> Sketch434 [N_Axis]
  Suppressed = false
  Type = 0
FEATURE [Sketcher::SketchObject] Sketch435
  ArcFitTolerance = 1e-06
  AttachmentOffset = pos=(-7,0,3) rot=(0,0,1;0rad)
  AttachmentSupport = -> [XZ_Plane283]
  FullyConstrained = true
  MakeInternals = false
  MapMode = 5
  Placement = pos=(-7,-3,7e-16) rot=(1,0,0;1.5708rad)
  sketch-geometry (7):
    g0: ArcOfCircle CenterX=10 CenterY=8 CenterZ=0 NormalX=0 NormalY=0 NormalZ=1 AngleXU=0 Radius=2 StartAngle=0 EndAngle=1.5708
    g1: LineSegment [constr] StartX=12 StartY=8 StartZ=0 EndX=12 EndY=10 EndZ=0
    g2: LineSegment [constr] StartX=12 StartY=10 StartZ=0 EndX=10 EndY=10 EndZ=0
    g3: LineSegment StartX=10 StartY=10 StartZ=0 EndX=16 EndY=10 EndZ=0
    g4: LineSegment StartX=16 StartY=10 StartZ=0 EndX=16 EndY=0 EndZ=0
    g5: LineSegment StartX=16 StartY=0 StartZ=0 EndX=12 EndY=0 EndZ=0
    g6: LineSegment StartX=12 StartY=0 StartZ=0 EndX=12 EndY=8 EndZ=0
  constraints (19):
    c: Tangent(g1,g0) = -1.5708
    c: Coincident(g2,g1)
    c: Horizontal(g2)
    c: Vertical(g1)
    c: Tangent(g2,g0) = -1.5708
    c: DistanceX(g2,g2) = 2
    c: DistanceX(g1) = 12
    c: DistanceY(g1) = 10
    c: Coincident(g0,g3)
    c: Coincident(g3,g4)
    c: Vertical(g4)
    c: Coincident(g4,g5)
    c: PointOnObject(g5,g-1)
    c: Horizontal(g5)
    c: Coincident(g5,g6)
    c: Coincident(g6,g0)
    c: Vertical(g6)
    c: Horizontal(g3)
    c: DistanceX(g5,g5) = 4
FEATURE [Sketcher::SketchObject] Sketch436
  ArcFitTolerance = 1e-06
  AttachmentSupport = -> [XZ_Plane283]
  FullyConstrained = true
  MakeInternals = false
  MapMode = 5
  Placement = pos=(0,0,0) rot=(1,0,0;1.5708rad)
  sketch-geometry (4):
    g0: LineSegment StartX=-6 StartY=6 StartZ=0 EndX=-6 EndY=-6 EndZ=0
    g1: LineSegment StartX=-6 StartY=-6 StartZ=0 EndX=6 EndY=-6 EndZ=0
    g2: LineSegment StartX=6 StartY=-6 StartZ=0 EndX=6 EndY=6 EndZ=0
    g3: LineSegment StartX=6 StartY=6 StartZ=0 EndX=-6 EndY=6 EndZ=0
  constraints (11):
    c: Coincident(g0,g1)
    c: Coincident(g1,g2)
    c: Coincident(g2,g3)
    c: Coincident(g3,g0)
    c: Vertical(g0)
    c: Vertical(g2)
    c: Horizontal(g1)
    c: Horizontal(g3)
    c: Symmetric(g2,g0,g-1)
    c: Equal(g3,g2)
    c: DistanceX(g3,g3) = 12
FEATURE [Sketcher::SketchObject] Sketch437
  ArcFitTolerance = 1e-06
  AttachmentOffset = pos=(0,0,3.7) rot=(0,0,1;0rad)
  AttachmentSupport = -> [XZ_Plane283]
  FullyConstrained = true
  MakeInternals = false
  MapMode = 5
  Placement = pos=(0,-3.7,8e-16) rot=(1,0,0;1.5708rad)
  sketch-geometry (1):
    g0: Circle CenterX=0 CenterY=0 CenterZ=0 NormalX=0 NormalY=0 NormalZ=1 AngleXU=0 Radius=2.75
  constraints (2):
    c: Coincident(g0,g-1)
    c: Diameter(g0) = 5.5
FEATURE [PartDesign::Pocket] Pocket305
  BaseFeature = -> Pad095
  Direction = (0,1,-2e-16)
  Length = 5
  Length2 = 5
  Placement = pos=(0,0,0) rot=(1,0,0;1.5708rad)
  Profile = -> Sketch437
  ReferenceAxis = -> Sketch437 [N_Axis]
  Suppressed = false
  Type = 1
FEATURE [PartDesign::Pocket] Pocket306
  BaseFeature = -> Pocket305
  Direction = (0,1,-2e-16)
  Length = 5
  Length2 = 5
  Placement = pos=(0,0,0) rot=(1,0,0;1.5708rad)
  Profile = -> Sketch436
  ReferenceAxis = -> Sketch436 [N_Axis]
  Refine = true
  Suppressed = false
  Type = 1
FEATURE [PartDesign::Groove] Groove016
  Angle = 90
  Angle2 = 60
  Axis = (0,2e-16,1)
  Base = (-7,-3,7e-16)
  BaseFeature = -> Pocket306
  Placement = pos=(0,0,0) rot=(1,0,0;1.5708rad)
  Profile = -> Sketch435
  ReferenceAxis = -> Sketch435 [V_Axis]
  Reversed = true
  Suppressed = false
  Type = 0
FEATURE [PartDesign::Pocket] Pocket307
  BaseFeature = -> Groove016
  Direction = (0,1,-2e-16)
  Length = 5
  Length2 = 5
  Placement = pos=(0,0,0) rot=(1,0,0;1.5708rad)
  Profile = -> Sketch435
  ReferenceAxis = -> Sketch435 [N_Axis]
  Suppressed = false
  Type = 1
FEATURE [PartDesign::Mirrored] Mirrored011
  BaseFeature = -> Pocket307
  MirrorPlane = -> XY_Plane283
  Originals = -> [Pocket307,Groove016]
  Placement = pos=(0,0,0) rot=(1,0,0;1.5708rad)
  Suppressed = false
  TransformMode = 0
FEATURE [PartDesign::Fillet] Fillet004
  Base = -> Mirrored011 [Edge75,Edge67]
  BaseFeature = -> Mirrored011
  Placement = pos=(0,0,0) rot=(1,0,0;1.5708rad)
  Radius = 1
  Refine = true
  SupportTransform = false
  Suppressed = false
  UseAllEdges = false
FEATURE [PartDesign::Chamfer] Chamfer007
  Angle = 45
  Base = -> Fillet004 [Edge5]
  BaseFeature = -> Fillet004
  ChamferType = 0
  FlipDirection = false
  Placement = pos=(0,0,0) rot=(1,0,0;1.5708rad)
  Size = 0.5
  Size2 = 1
  SupportTransform = false
  Suppressed = false
  UseAllEdges = false
FEATURE [PartDesign::Body] Body146  label="hinge-stat-drv"
  AllowCompound = false
  Group = -> [Sketch431,Pad094,Sketch432,Pocket301,Sketch433,Pocket302,Sketch434,Pad095,Sketch435,Sketch436,Sketch437,Pocket305,Pocket306,Groove016,Pocket307,Mirrored011,Fillet004,Chamfer007]
  Origin = -> Origin284
  Tip = -> Chamfer007
COMPONENT P10 — recipe-attached ("hinge-mov-drv", modeled in this document).
Construction recipe (the document's own serialized feature program — sketch geometry with constraints, then the solid features built on it; lengths are millimeters unless a unit is written):

FEATURE [Sketcher::SketchObject] Sketch438
  ArcFitTolerance = 1e-06
  AttachmentSupport = -> [XZ_Plane284]
  FullyConstrained = true
  MakeInternals = false
  MapMode = 5
  Placement = pos=(0,0,0) rot=(1,0,0;1.5708rad)
  sketch-geometry (16):
    g0: LineSegment [constr] StartX=-11 StartY=16 StartZ=0 EndX=-11 EndY=-16 EndZ=0
    g1: LineSegment [constr] StartX=-11 StartY=-16 StartZ=0 EndX=10 EndY=-16 EndZ=0
    g2: LineSegment [constr] StartX=10 StartY=-16 StartZ=0 EndX=10 EndY=16 EndZ=0
    g3: LineSegment [constr] StartX=10 StartY=16 StartZ=0 EndX=-11 EndY=16 EndZ=0
    g4: LineSegment StartX=3.3 StartY=10.3 StartZ=0 EndX=-11 EndY=10.3 EndZ=0
    g5: LineSegment StartX=-11 StartY=10.3 StartZ=0 EndX=-11 EndY=16 EndZ=0
    g6: LineSegment StartX=-11 StartY=16 StartZ=0 EndX=10 EndY=16 EndZ=0
    g7: LineSegment StartX=10 StartY=16 StartZ=0 EndX=10 EndY=-16 EndZ=0
    g8: LineSegment StartX=10 StartY=-16 StartZ=0 EndX=-11 EndY=-16 EndZ=0
    g9: LineSegment StartX=-11 StartY=-16 StartZ=0 EndX=-11 EndY=-10.3 EndZ=0
    g10: LineSegment StartX=-11 StartY=-10.3 StartZ=0 EndX=3.3 EndY=-10.3 EndZ=0
    g11: LineSegment StartX=5.3 StartY=-8.3 StartZ=0 EndX=5.3 EndY=8.3 EndZ=0
    g12: ArcOfCircle CenterX=3.3 CenterY=8.3 CenterZ=0 NormalX=0 NormalY=0 NormalZ=1 AngleXU=0 Radius=2 StartAngle=0 EndAngle=1.5708
    g13: GeomPoint [constr] X=5.3 Y=10.3 Z=0
    g14: ArcOfCircle CenterX=3.3 CenterY=-8.3 CenterZ=0 NormalX=0 NormalY=0 NormalZ=1 AngleXU=0 Radius=2 StartAngle=4.71239 EndAngle=6.28319
    g15: GeomPoint [constr] X=5.3 Y=-10.3 Z=0
  constraints (38):
    c: Coincident(g0,g1)
    c: Coincident(g1,g2)
    c: Coincident(g2,g3)
    c: Coincident(g3,g0)
    c: Vertical(g0)
    c: Horizontal(g1)
    c: Horizontal(g3)
    c: DistanceX(g3,g3) = 21
    c: DistanceY(g2,g2) = 32
    c: PointOnObject(g4,g0)
    c: Horizontal(g4)
    c: Coincident(g4,g5)
    c: Coincident(g5,g0)
    c: Coincident(g5,g6)
    c: Coincident(g6,g2)
    c: Coincident(g6,g7)
    c: Coincident(g7,g1)
    c: Coincident(g7,g8)
    c: Coincident(g8,g0)
    c: Coincident(g8,g9)
    c: PointOnObject(g9,g0)
    c: Coincident(g9,g10)
    c: Horizontal(g10)
    c: Symmetric(g13,g15,g-1)
    c: DistanceX(g15) = 5.3
    c: DistanceY(g13) = 10.3
    c: DistanceX(g2) = 10
    c: Symmetric(g2,g1,g-1)
    c: PointOnObject(g13,g4)
    c: PointOnObject(g13,g11)
    c: Tangent(g4,g12) = -1.5708
    c: Tangent(g11,g12) = -1.5708
    c: PointOnObject(g15,g10)
    c: PointOnObject(g15,g11)
    c: Tangent(g10,g14) = -1.5708
    c: Tangent(g11,g14) = -1.5708
    c: Equal(g14,g12)
    c: Radius(g12) = 2
FEATURE [PartDesign::Pad] Pad096
  Direction = (0,-1,2e-16)
  Length = 8
  Length2 = 10
  Placement = pos=(0,0,0) rot=(1,0,0;1.5708rad)
  Profile = -> Sketch438
  ReferenceAxis = -> Sketch438 [N_Axis]
  Suppressed = false
  Type = 0
FEATURE [Sketcher::SketchObject] Sketch439
  ArcFitTolerance = 1e-06
  AttachmentOffset = pos=(0,0,8) rot=(0,0,1;0rad)
  AttachmentSupport = -> [XZ_Plane284]
  FullyConstrained = true
  MakeInternals = false
  MapMode = 5
  Placement = pos=(0,-8,1.8e-15) rot=(1,0,0;1.5708rad)
  sketch-geometry (12):
    g0: LineSegment StartX=-4 StartY=16 StartZ=0 EndX=-4 EndY=24 EndZ=0
    g1: LineSegment StartX=-4 StartY=24 StartZ=0 EndX=12 EndY=24 EndZ=0
    g2: LineSegment StartX=20 StartY=16 StartZ=0 EndX=20 EndY=-16 EndZ=0
    g3: LineSegment StartX=12 StartY=-24 StartZ=0 EndX=-4 EndY=-24 EndZ=0
    g4: LineSegment StartX=-4 StartY=-24 StartZ=0 EndX=-4 EndY=-16 EndZ=0
    g5: LineSegment StartX=-4 StartY=-16 StartZ=0 EndX=10 EndY=-16 EndZ=0
    g6: LineSegment StartX=10 StartY=-16 StartZ=0 EndX=10 EndY=16 EndZ=0
    g7: LineSegment StartX=10 StartY=16 StartZ=0 EndX=-4 EndY=16 EndZ=0
    g8: ArcOfCircle CenterX=12 CenterY=16 CenterZ=0 NormalX=0 NormalY=0 NormalZ=1 AngleXU=0 Radius=8 StartAngle=0 EndAngle=1.5708
    g9: GeomPoint [constr] X=20 Y=24 Z=0
    g10: ArcOfCircle CenterX=12 CenterY=-16 CenterZ=0 NormalX=0 NormalY=0 NormalZ=1 AngleXU=0 Radius=8 StartAngle=4.71239 EndAngle=6.28319
    g11: GeomPoint [constr] X=20 Y=-24 Z=0
  constraints (30):
    c: Vertical(g0)
    c: Coincident(g0,g1)
    c: Horizontal(g1)
    c: Vertical(g2)
    c: Horizontal(g3)
    c: Coincident(g3,g4)
    c: Coincident(g4,g5)
    c: Horizontal(g5)
    c: Coincident(g5,g6)
    c: Vertical(g6)
    c: Coincident(g6,g7)
    c: Coincident(g7,g0)
    c: Symmetric(g4,g0,g-1)
    c: Symmetric(g0,g3,g-1)
    c: DistanceY(g6,g9) = 8
    c: DistanceY(g6,g6) = 32
    c: PointOnObject(g9,g1)
    c: PointOnObject(g9,g2)
    c: Tangent(g1,g8) = 1.5708
    c: Tangent(g2,g8) = 1.5708
    c: PointOnObject(g11,g2)
    c: PointOnObject(g11,g3)
    c: Tangent(g2,g10) = 1.5708
    c: Tangent(g3,g10) = 1.5708
    c: Radius(g8) = 8
    c: Equal(g10,g8)
    c: DistanceX(g0) = -4
    c: DistanceX(g8) = 12
    c: Horizontal(g7)
    c: DistanceX(g6) = 10
FEATURE [PartDesign::Pad] Pad097
  BaseFeature = -> Pad096
  Direction = (0,-1,2e-16)
  Length = 5
  Length2 = 10
  Placement = pos=(0,0,0) rot=(1,0,0;1.5708rad)
  Profile = -> Sketch439
  ReferenceAxis = -> Sketch439 [N_Axis]
  Refine = true
  Reversed = true
  Suppressed = false
  Type = 0
FEATURE [Sketcher::SketchObject] Sketch440
  ArcFitTolerance = 1e-06
  AttachmentSupport = -> [XY_Plane284]
  FullyConstrained = true
  MakeInternals = false
  MapMode = 5
  sketch-geometry (6):
    g0: ArcOfCircle CenterX=-7 CenterY=-4 CenterZ=0 NormalX=0 NormalY=0 NormalZ=1 AngleXU=0 Radius=4 StartAngle=1.57079 EndAngle=3.92699
    g1: LineSegment StartX=-8.65685 StartY=-8 StartZ=0 EndX=-12 EndY=-8 EndZ=0
    g2: LineSegment StartX=-12 StartY=-8 StartZ=0 EndX=-12 EndY=0 EndZ=0
    g3: LineSegment StartX=-12 StartY=0 StartZ=0 EndX=-6.99998 EndY=-3.95386e-11 EndZ=0
    g4: LineSegment StartX=-9.82843 StartY=-6.82843 StartZ=0 EndX=-8.65685 EndY=-8 EndZ=0
    g5: Circle CenterX=-7 CenterY=-4 CenterZ=0 NormalX=0 NormalY=0 NormalZ=1 AngleXU=0 Radius=1.6
  constraints (17):
    c: PointOnObject(g0,g-1)
    c: Coincident(g1,g2)
    c: PointOnObject(g2,g-1)
    c: Vertical(g2)
    c: Coincident(g2,g3)
    c: Coincident(g3,g0)
    c: Tangent(g3,g0)
    c: Diameter(g0) = 8
    c: Horizontal(g1)
    c: DistanceX(g0) = -7
    c: DistanceX(g3,g3) = 5
    c: Coincident(g4,g1)
    c: Tangent(g4,g0) = -1.5708
    c: Tangent(g1,g0)
    c: Angle(g4) = -0.785398
    c: Coincident(g5,g0)
    c: Diameter(g5) = 3.2
FEATURE [PartDesign::Pocket] Pocket308
  BaseFeature = -> Pad097
  Direction = (0,0,-1)
  Length = 5
  Length2 = 5
  Midplane = true
  Placement = pos=(0,0,0) rot=(1,0,0;1.5708rad)
  Profile = -> Sketch440
  ReferenceAxis = -> Sketch440 [N_Axis]
  Suppressed = false
  Type = 1
FEATURE [PartDesign::Fillet] Fillet005
  Base = -> Pocket308 [Edge55,Edge52]
  BaseFeature = -> Pocket308
  Placement = pos=(0,0,0) rot=(1,0,0;1.5708rad)
  Radius = 2
  SupportTransform = false
  Suppressed = false
  UseAllEdges = false
FEATURE [PartDesign::Fillet] Fillet006
  Base = -> Fillet005 [Edge61,Edge73,Edge54,Edge53,Edge57,Edge4,Edge9]
  BaseFeature = -> Fillet005
  Placement = pos=(0,0,0) rot=(1,0,0;1.5708rad)
  Radius = 1
  SupportTransform = false
  Suppressed = false
  UseAllEdges = false
FEATURE [Sketcher::SketchObject] Sketch441
  ArcFitTolerance = 1e-06
  AttachmentOffset = pos=(0,0,8) rot=(0,0,1;0rad)
  AttachmentSupport = -> [XZ_Plane284]
  FullyConstrained = true
  MakeInternals = false
  MapMode = 5
  Placement = pos=(0,-8,1.8e-15) rot=(1,0,0;1.5708rad)
  sketch-geometry (21):
    g0: LineSegment StartX=3.17543 StartY=20 StartZ=0 EndX=1.58771 EndY=22.75 EndZ=0
    g1: LineSegment StartX=1.58771 StartY=22.75 StartZ=0 EndX=-1.58771 EndY=22.75 EndZ=0
    g2: LineSegment StartX=-1.58771 StartY=22.75 StartZ=0 EndX=-3.17543 EndY=20 EndZ=0
    g3: LineSegment StartX=-3.17543 StartY=20 StartZ=0 EndX=-1.58771 EndY=17.25 EndZ=0
    g4: LineSegment StartX=-1.58771 StartY=17.25 StartZ=0 EndX=1.58771 EndY=17.25 EndZ=0
    g5: LineSegment StartX=1.58771 StartY=17.25 StartZ=0 EndX=3.17543 EndY=20 EndZ=0
    g6: Circle [constr] CenterX=0 CenterY=20 CenterZ=0 NormalX=0 NormalY=0 NormalZ=1 AngleXU=0 Radius=3.17543
    g7: LineSegment StartX=1.58771 StartY=-22.75 StartZ=0 EndX=3.17543 EndY=-20 EndZ=0
    g8: LineSegment StartX=3.17543 StartY=-20 StartZ=0 EndX=1.58771 EndY=-17.25 EndZ=0
    g9: LineSegment StartX=1.58771 StartY=-17.25 StartZ=0 EndX=-1.58771 EndY=-17.25 EndZ=0
    g10: LineSegment StartX=-1.58771 StartY=-17.25 StartZ=0 EndX=-3.17543 EndY=-20 EndZ=0
    g11: LineSegment StartX=-3.17543 StartY=-20 StartZ=0 EndX=-1.58771 EndY=-22.75 EndZ=0
    g12: LineSegment StartX=-1.58771 StartY=-22.75 StartZ=0 EndX=1.58771 EndY=-22.75 EndZ=0
    g13: Circle [constr] CenterX=0 CenterY=-20 CenterZ=0 NormalX=0 NormalY=0 NormalZ=1 AngleXU=0 Radius=3.17543
    g14: LineSegment StartX=13.4123 StartY=-2.75 StartZ=0 EndX=16.5877 EndY=-2.75 EndZ=0
    g15: LineSegment StartX=16.5877 StartY=-2.75 StartZ=0 EndX=18.1754 EndY=0 EndZ=0
    g16: LineSegment StartX=18.1754 StartY=0 StartZ=0 EndX=16.5877 EndY=2.75 EndZ=0
    g17: LineSegment StartX=16.5877 StartY=2.75 StartZ=0 EndX=13.4123 EndY=2.75 EndZ=0
    g18: LineSegment StartX=13.4123 StartY=2.75 StartZ=0 EndX=11.8246 EndY=0 EndZ=0
    g19: LineSegment StartX=11.8246 StartY=-1e-16 StartZ=0 EndX=13.4123 EndY=-2.75 EndZ=0
    g20: Circle [constr] CenterX=15 CenterY=0 CenterZ=0 NormalX=0 NormalY=0 NormalZ=1 AngleXU=0 Radius=3.17543
  constraints (50):
    c: Coincident(g0,g1)
    c: Coincident(g1,g2)
    c: Coincident(g2,g3)
    c: Coincident(g3,g4)
    c: Coincident(g4,g5)
    c: Coincident(g5,g0)
    c: Equal(g0, g1-g5) x5
    c: PointOnObject(g0,g6)
    c: PointOnObject(g1,g6)
    c: PointOnObject(g2,g6)
    c: PointOnObject(g3,g6)
    c: PointOnObject(g4,g6)
    c: PointOnObject(g5,g6)
    c: Coincident(g7,g8)
    c: Coincident(g8,g9)
    c: Coincident(g9,g10)
    c: Coincident(g10,g11)
    c: Coincident(g11,g12)
    c: Coincident(g12,g7)
    c: Equal(g7, g8-g12) x5
    c: PointOnObject(g7,g13)
    c: PointOnObject(g8,g13)
    c: PointOnObject(g9,g13)
    c: PointOnObject(g10,g13)
    c: PointOnObject(g11,g13)
    c: PointOnObject(g12,g13)
    c: Symmetric(g13,g6,g-1)
    c: Horizontal(g1)
    c: Horizontal(g9)
    c: Equal(g13,g6)
    c: DistanceY(g13) = -20
    c: DistanceY(g4,g0) = 5.5
    c: DistanceX(g13) = 0
    c: Coincident(g14,g15)
    c: Coincident(g15,g16)
    c: Coincident(g16,g17)
    c: Coincident(g17,g18)
    c: Coincident(g18,g19)
    c: Coincident(g19,g14)
    c: Equal(g14, g15-g19) x5
    c: PointOnObject(g14,g20)
    c: PointOnObject(g15,g20)
    c: PointOnObject(g16,g20)
    c: PointOnObject(g17,g20)
    c: PointOnObject(g18,g20)
    c: PointOnObject(g19,g20)
    c: PointOnObject(g20,g-1)
    c: Equal(g20,g13)
    c: DistanceX(g20) = 15
    c: Horizontal(g17)
FEATURE [PartDesign::Pocket] Pocket309
  BaseFeature = -> Fillet006
  Direction = (0,1,-2e-16)
  Length = 3
  Length2 = 5
  Placement = pos=(0,0,0) rot=(1,0,0;1.5708rad)
  Profile = -> Sketch441
  ReferenceAxis = -> Sketch441 [N_Axis]
  Suppressed = false
  Type = 0
FEATURE [Sketcher::SketchObject] Sketch442
  ArcFitTolerance = 1e-06
  AttachmentOffset = pos=(0,0,4.7) rot=(0,0,1;0rad)
  AttachmentSupport = -> [XZ_Plane284]
  FullyConstrained = true
  MakeInternals = false
  MapMode = 5
  Placement = pos=(0,-4.7,1e-15) rot=(1,0,0;1.5708rad)
  sketch-geometry (3):
    g0: Circle CenterX=0 CenterY=20 CenterZ=0 NormalX=0 NormalY=0 NormalZ=1 AngleXU=0 Radius=1.75
    g1: Circle CenterX=15 CenterY=0 CenterZ=0 NormalX=0 NormalY=0 NormalZ=1 AngleXU=0 Radius=1.75
    g2: Circle CenterX=0 CenterY=-20 CenterZ=0 NormalX=0 NormalY=0 NormalZ=1 AngleXU=0 Radius=1.75
  constraints (8):
    c: PointOnObject(g1,g-1)
    c: Symmetric(g2,g0,g-1)
    c: Equal(g0,g1)
    c: Equal(g1,g2)
    c: DistanceX(g1) = 15
    c: DistanceX(g0) = 0
    c: DistanceY(g0) = 20
    c: Diameter(g1) = 3.5
FEATURE [PartDesign::Pocket] Pocket310
  BaseFeature = -> Pocket309
  Direction = (0,1,-2e-16)
  Length = 5
  Length2 = 5
  Placement = pos=(0,0,0) rot=(1,0,0;1.5708rad)
  Profile = -> Sketch442
  ReferenceAxis = -> Sketch442 [N_Axis]
  Suppressed = false
  Type = 1
FEATURE [PartDesign::Chamfer] Chamfer008
  Angle = 45
  Base = -> Pocket310 [Face33]
  BaseFeature = -> Pocket310
  ChamferType = 0
  FlipDirection = false
  Placement = pos=(0,0,0) rot=(1,0,0;1.5708rad)
  Size = 0.3
  Size2 = 1
  SupportTransform = false
  Suppressed = false
  UseAllEdges = false
FEATURE [PartDesign::Body] Body147  label="hinge-mov-drv"
  AllowCompound = false
  Group = -> [Sketch438,Pad096,Sketch439,Pad097,Sketch440,Pocket308,Fillet005,Fillet006,Sketch441,Pocket309,Sketch442,Pocket310,Chamfer008]
  Origin = -> Origin285
  Tip = -> Chamfer008
COMPONENT P11 — recipe-attached ("rail-mgn9-250-drv", modeled in this document).
Construction recipe (the document's own serialized feature program — sketch geometry with constraints, then the solid features built on it; lengths are millimeters unless a unit is written):

FEATURE [Sketcher::SketchObject] Sketch467
  ArcFitTolerance = 1e-06
  AttachmentSupport = -> [XZ_Plane292]
  FullyConstrained = true
  MakeInternals = false
  MapMode = 5
  Placement = pos=(0,0,0) rot=(1,0,0;1.5708rad)
  sketch-geometry (4):
    g0: LineSegment StartX=-4.5 StartY=0 StartZ=0 EndX=4.5 EndY=0 EndZ=0
    g1: LineSegment StartX=4.5 StartY=0 StartZ=0 EndX=4.5 EndY=6 EndZ=0
    g2: LineSegment StartX=4.5 StartY=6 StartZ=0 EndX=-4.5 EndY=6 EndZ=0
    g3: LineSegment StartX=-4.5 StartY=6 StartZ=0 EndX=-4.5 EndY=0 EndZ=0
  constraints (11):
    c: Coincident(g0,g1)
    c: Coincident(g1,g2)
    c: Coincident(g2,g3)
    c: Coincident(g3,g0)
    c: Horizontal(g0)
    c: Vertical(g1)
    c: Vertical(g3)
    c: PointOnObject(g0,g-1)
    c: DistanceY(g1,g1) = 6
    c: Symmetric(g1,g2,g-2)
    c: DistanceX(g2,g2) = 9
FEATURE [PartDesign::Pad] Pad101
  Direction = (0,-1,2e-16)
  Length = 250
  Length2 = 10
  Placement = pos=(0,0,0) rot=(1,0,0;1.5708rad)
  Profile = -> Sketch467
  ReferenceAxis = -> Sketch467 [N_Axis]
  Suppressed = false
  Type = 0
FEATURE [PartDesign::Body] Body153  label="rail-mgn9-250-drv"
  AllowCompound = false
  Group = -> [Sketch467,Pad101]
  Origin = -> Origin293
  Tip = -> Pad101
COMPONENT P12 — recipe-attached ("carriage-mgn9h-drv", modeled in this document).
Construction recipe (the document's own serialized feature program — sketch geometry with constraints, then the solid features built on it; lengths are millimeters unless a unit is written):

FEATURE [Sketcher::SketchObject] Sketch468
  ArcFitTolerance = 1e-06
  AttachmentSupport = -> [XZ_Plane293]
  FullyConstrained = true
  MakeInternals = false
  MapMode = 5
  Placement = pos=(0,0,0) rot=(1,0,0;1.5708rad)
  sketch-geometry (8):
    g0: LineSegment StartX=-10 StartY=10 StartZ=0 EndX=-10 EndY=2 EndZ=0
    g1: LineSegment StartX=-10 StartY=2 StartZ=0 EndX=-5 EndY=2 EndZ=0
    g2: LineSegment StartX=10 StartY=2 StartZ=0 EndX=10 EndY=10 EndZ=0
    g3: LineSegment StartX=10 StartY=10 StartZ=0 EndX=-10 EndY=10 EndZ=0
    g4: LineSegment StartX=-5 StartY=2 StartZ=0 EndX=-5 EndY=6.5 EndZ=0
    g5: LineSegment StartX=-5 StartY=6.5 StartZ=0 EndX=5 EndY=6.5 EndZ=0
    g6: LineSegment StartX=5 StartY=6.5 StartZ=0 EndX=5 EndY=2 EndZ=0
    g7: LineSegment StartX=5 StartY=2 StartZ=0 EndX=10 EndY=2 EndZ=0
  constraints (23):
    c: Coincident(g0,g1)
    c: Coincident(g7,g2)
    c: Coincident(g2,g3)
    c: Coincident(g3,g0)
    c: Vertical(g0)
    c: Vertical(g2)
    c: Horizontal(g1)
    c: Symmetric(g2,g0,g-2)
    c: DistanceX(g3,g3) = 20
    c: DistanceY(g2) = 10
    c: DistanceY(g7) = 2
    c: Vertical(g4)
    c: Coincident(g4,g5)
    c: Coincident(g5,g6)
    c: PointOnObject(g6,g7)
    c: Vertical(g6)
    c: Coincident(g1,g4)
    c: PointOnObject(g7,g6)
    c: Symmetric(g5,g4,g-2)
    c: DistanceX(g5,g5) = 10
    c: DistanceY(g5) = 6.5
    c: Horizontal(g7)
    c: Horizontal(g1,g6)
FEATURE [PartDesign::Pad] Pad102
  Direction = (0,-1,2e-16)
  Length = 39
  Length2 = 10
  Midplane = true
  Placement = pos=(0,0,0) rot=(1,0,0;1.5708rad)
  Profile = -> Sketch468
  ReferenceAxis = -> Sketch468 [N_Axis]
  Suppressed = false
  Type = 0
FEATURE [PartDesign::Body] Body154  label="carriage-mgn9h-drv"
  AllowCompound = false
  Group = -> [Sketch468,Pad102]
  Origin = -> Origin294
  Tip = -> Pad102
